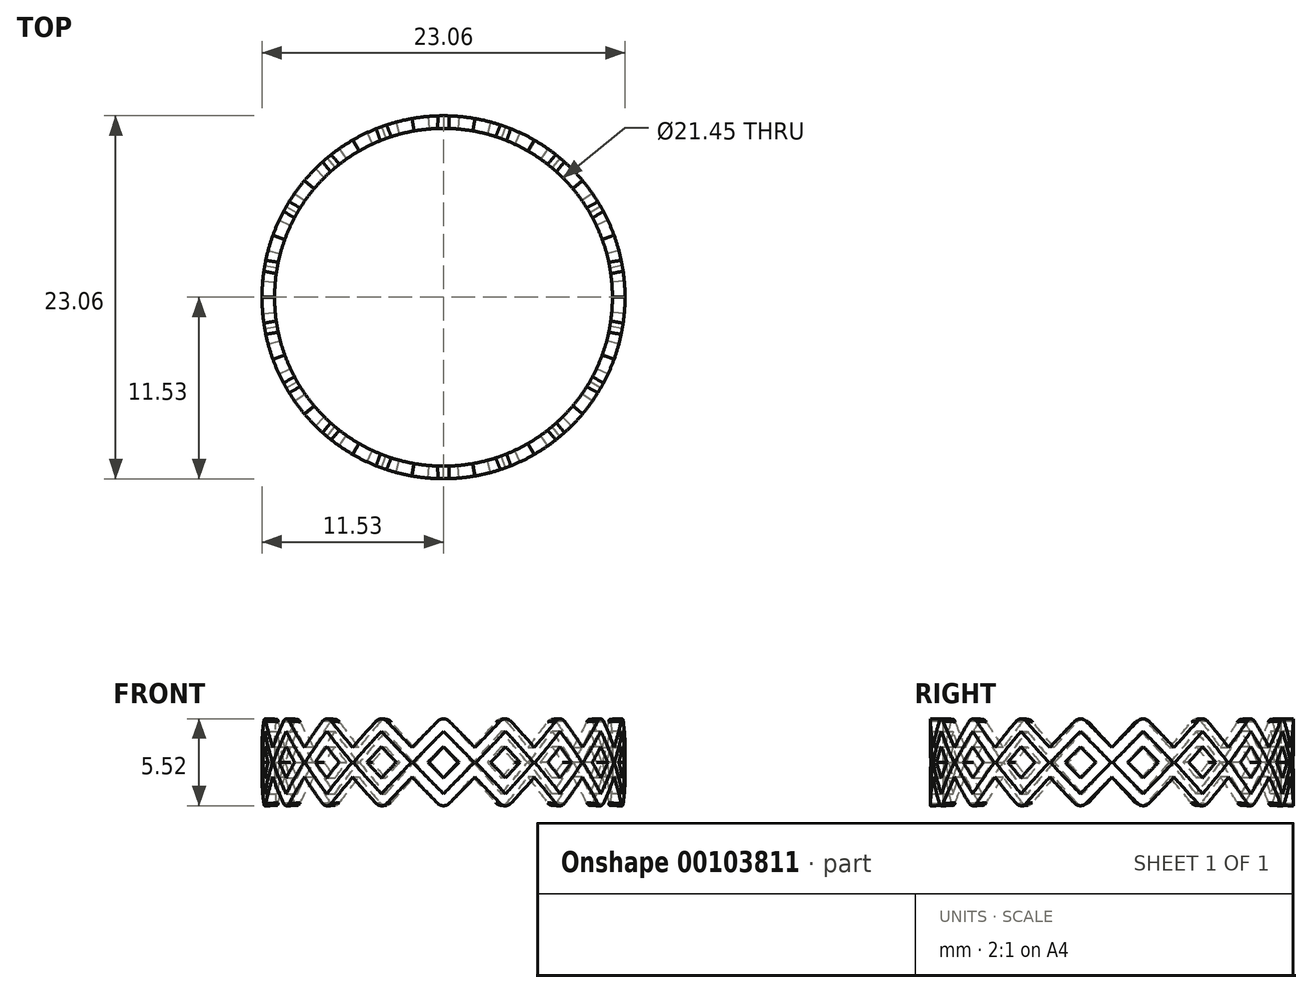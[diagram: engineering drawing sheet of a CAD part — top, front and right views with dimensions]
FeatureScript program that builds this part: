
annotation { "Feature Type Name" : "Feature", "Feature Type Description" : "" }
export const myFeature = defineFeature(function(context is Context, id is Id, definition is map)
    precondition{}
    {
        {
            var Q0;
            Q0=qCreatedBy(makeId("Front.planeOp"),FACE);
            var sketch = newSketch(context, id + "F0", { "sketchPlane" : qUnion([Q0])});
            skLineSegment(sketch, "E0", {"start": v(0, 0) * mm, "end": v(0, 10) * mm, "construction": true});
            skSolve(sketch);
        }
        {
            var Q0;
            Q0=qCreatedBy(makeId("Front.planeOp"),FACE);
            cPlane(context, id + "F1", {"entities" : qUnion([Q0]), "cplaneType" : CPlaneType.OFFSET, "offset" : 11.53 * mm, "width" : 150 * mm, "height" : 150 * mm});
        }
        {
            var Q0;
            Q0=qCreatedBy(makeId("Front.planeOp"),FACE);
            cPlane(context, id + "F2", {"entities" : qUnion([Q0]), "cplaneType" : CPlaneType.OFFSET, "offset" : 9 * mm, "width" : 150 * mm, "height" : 150 * mm});
        }
        {
            var Q0;
            Q0=qCreatedBy(makeId("Top.planeOp"),FACE);
            var sketch = newSketch(context, id + "F3", { "sketchPlane" : qUnion([Q0])});
            skLineSegment(sketch, "E1", {"start": v(0, 0) * mm, "end": v(10.03, 0) * mm, "construction": true});
            skLineSegment(sketch, "E2", {"start": v(10.03, 0) * mm, "end": v(11.53, 0) * mm, "construction": true});
            skCircle(sketch, "E3", {"center": v(0, 0) * mm, "radius": 10.03 * mm});
            skCircle(sketch, "E4", {"center": v(0, 0) * mm, "radius": 11.53 * mm});
            skSolve(sketch);
        }
        {
            var Q0;
            Q0=qCreatedBy(makeId("Top.planeOp"),FACE);
            var sketch = newSketch(context, id + "F4", { "sketchPlane" : qUnion([Q0])});
            skLineSegment(sketch, "E5", {"start": v(0, 0) * mm, "end": v(10.73, 0) * mm});
            skLineSegment(sketch, "E6", {"start": v(10.73, 0) * mm, "end": v(11.53, 0) * mm});
            skCircle(sketch, "E7", {"center": v(0, 0) * mm, "radius": 11.53 * mm});
            skCircle(sketch, "E8", {"center": v(0, 0) * mm, "radius": 10.73 * mm});
            skSolve(sketch);
        }
        {
            var Q0;
            Q0=qCreatedBy(id+"F1.planeOp",FACE);
            var sketch = newSketch(context, id + "F5", { "sketchPlane" : qUnion([Q0])});
            skLineSegment(sketch, "E9", {"start": v(-2.97, 0) * mm, "end": v(0, 2.97) * mm});
            skLineSegment(sketch, "E10", {"start": v(0, 2.97) * mm, "end": v(2.97, 0) * mm});
            skLineSegment(sketch, "E11", {"start": v(2.97, 0) * mm, "end": v(0, -2.97) * mm});
            skLineSegment(sketch, "E12", {"start": v(0, -2.97) * mm, "end": v(-2.97, 0) * mm});
            skSolve(sketch);
        }
        {
            var Q0;
            Q0=qCreatedBy(id+"F1.planeOp",FACE);
            var sketch = newSketch(context, id + "F6", { "sketchPlane" : qUnion([Q0])});
            skLineSegment(sketch, "E13", {"start": v(0, 1.96) * mm, "end": v(-1.98, -0.02) * mm});
            skLineSegment(sketch, "E14", {"start": v(-1.98, -0.02) * mm, "end": v(0, -2) * mm});
            skLineSegment(sketch, "E15", {"start": v(0, -2) * mm, "end": v(1.98, -0.02) * mm});
            skLineSegment(sketch, "E16", {"start": v(0, 1.96) * mm, "end": v(1.98, -0.02) * mm});
            skSolve(sketch);
        }
        {
            var Q0;
            Q0=qCreatedBy(id+"F1.planeOp",FACE);
            var sketch = newSketch(context, id + "F7", { "sketchPlane" : qUnion([Q0])});
            skLineSegment(sketch, "E17", {"start": v(-0.99, 0) * mm, "end": v(0, 0.99) * mm});
            skLineSegment(sketch, "E18", {"start": v(0, 0.99) * mm, "end": v(0.99, 0) * mm});
            skLineSegment(sketch, "E19", {"start": v(0.99, 0) * mm, "end": v(0, -0.99) * mm});
            skLineSegment(sketch, "E20", {"start": v(0, -0.99) * mm, "end": v(-0.99, 0) * mm});
            skSolve(sketch);
        }
        {
            var Q0;
            Q0=qCreatedBy(makeId("Top.planeOp"),FACE);
            var sketch = newSketch(context, id + "F8", { "sketchPlane" : qUnion([Q0])});
            skLineSegment(sketch, "E21", {"start": v(0, 0) * mm, "end": v(0, 0) * mm});
            skLineSegment(sketch, "E22", {"start": v(0, 0) * mm, "end": v(-0.77, -9) * mm, "construction": true});
            skLineSegment(sketch, "E23", {"start": v(0, 0) * mm, "end": v(0.77, -9) * mm, "construction": true});
            skLineSegment(sketch, "E24", {"start": v(-0.77, -9) * mm, "end": v(-0.99, -11.53) * mm, "construction": true});
            skLineSegment(sketch, "E25", {"start": v(0.77, -9) * mm, "end": v(0.99, -11.53) * mm, "construction": true});
            skSolve(sketch);
        }
        {
            var Q0;
            Q0=qCreatedBy(makeId("Top.planeOp"),FACE);
            var sketch = newSketch(context, id + "F9", { "sketchPlane" : qUnion([Q0])});
            skLineSegment(sketch, "E26", {"start": v(0, 0) * mm, "end": v(2.32, -9) * mm, "construction": true});
            skLineSegment(sketch, "E27", {"start": v(0, 0) * mm, "end": v(-2.32, -9) * mm, "construction": true});
            skLineSegment(sketch, "E28", {"start": v(2.32, -9) * mm, "end": v(2.97, -11.53) * mm, "construction": true});
            skLineSegment(sketch, "E29", {"start": v(-2.32, -9) * mm, "end": v(-2.97, -11.53) * mm, "construction": true});
            skSolve(sketch);
        }
        {
            var Q0;
            Q0=qCreatedBy(id+"F2.planeOp",FACE);
            var sketch = newSketch(context, id + "F10", { "sketchPlane" : qUnion([Q0])});
            skLineSegment(sketch, "E30", {"start": v(0, 2.97) * mm, "end": v(-2.32, 0) * mm});
            skLineSegment(sketch, "E31", {"start": v(-2.32, 0) * mm, "end": v(0, -2.97) * mm});
            skLineSegment(sketch, "E32", {"start": v(0, -2.97) * mm, "end": v(2.32, 0) * mm});
            skLineSegment(sketch, "E33", {"start": v(2.32, 0) * mm, "end": v(0, 2.97) * mm});
            skSolve(sketch);
        }
        {
            var Q0;
            Q0=qCreatedBy(id+"F2.planeOp",FACE);
            var sketch = newSketch(context, id + "F11", { "sketchPlane" : qUnion([Q0])});
            skLineSegment(sketch, "E34", {"start": v(0, 1.96) * mm, "end": v(-1.55, 0) * mm});
            skLineSegment(sketch, "E35", {"start": v(-1.55, 0) * mm, "end": v(0, -2) * mm});
            skLineSegment(sketch, "E36", {"start": v(0, -2) * mm, "end": v(1.55, 0) * mm});
            skLineSegment(sketch, "E37", {"start": v(1.55, 0) * mm, "end": v(0, 1.96) * mm});
            skSolve(sketch);
        }
        {
            var Q0;
            Q0=qCreatedBy(id+"F2.planeOp",FACE);
            var sketch = newSketch(context, id + "F12", { "sketchPlane" : qUnion([Q0])});
            skLineSegment(sketch, "E38", {"start": v(0, 0.99) * mm, "end": v(-0.77, 0) * mm});
            skLineSegment(sketch, "E39", {"start": v(-0.77, 0) * mm, "end": v(0, -0.99) * mm});
            skLineSegment(sketch, "E40", {"start": v(0, -0.99) * mm, "end": v(0.77, 0) * mm});
            skLineSegment(sketch, "E41", {"start": v(0.77, 0) * mm, "end": v(0, 0.99) * mm});
            skSolve(sketch);
        }
        {
            var Q0;
            Q0=makeQuery(id+"F5.imprint","IMPRINT",FACE,{"disambiguationData":[TD([[makeQuery(id+"F5.imprint","IMPRINT",EDGE,{"derivedFrom":sQuery(id+"F5.wireOp",EDGE,"E9")}),-1.0]])]});
            var Q1;
            Q1=makeQuery(id+"F10.imprint","IMPRINT",FACE,{"disambiguationData":[TD([[makeQuery(id+"F10.imprint","IMPRINT",EDGE,{"derivedFrom":sQuery(id+"F10.wireOp",EDGE,"E30")}),1.0]])]});
            loft(context, id + "F13", {"sheetProfilesArray" : [{ "sheetProfileEntities" : qUnion([Q0]) }, { "sheetProfileEntities" : qUnion([Q1]) }]});
        }
        {
            var Q0;
            Q0=makeQuery(id+"F6.imprint","IMPRINT",FACE,{"disambiguationData":[TD([[makeQuery(id+"F6.imprint","IMPRINT",EDGE,{"derivedFrom":sQuery(id+"F6.wireOp",EDGE,"E13")}),1.0]])]});
            var Q1;
            Q1=makeQuery(id+"F11.imprint","IMPRINT",FACE,{"disambiguationData":[TD([[makeQuery(id+"F11.imprint","IMPRINT",EDGE,{"derivedFrom":sQuery(id+"F11.wireOp",EDGE,"E34")}),1.0]])]});
            loft(context, id + "F14", {"sheetProfilesArray" : [{ "sheetProfileEntities" : qUnion([Q0]) }, { "sheetProfileEntities" : qUnion([Q1]) }]});
        }
        {
            var Q0;
            Q0 = qSketchRegion(id + "F7", true);
            var Q1;
            Q1 = qSketchRegion(id + "F12", true);
            loft(context, id + "F15", {"sheetProfilesArray" : [{ "sheetProfileEntities" : qUnion([Q0]) }, { "sheetProfileEntities" : qUnion([Q1]) }]});
        }
        {
            var Q0;
            Q0=makeQuery(id+"F13.opLoft","SWEPT_BODY",BODY,{"disambiguationData":[OSD([makeQuery(id+"F5.imprint","IMPRINT",FACE,{"disambiguationData":[TD([[makeQuery(id+"F5.imprint","IMPRINT",EDGE,{"derivedFrom":sQuery(id+"F5.wireOp",EDGE,"E9")}),-1.0]])]}),makeQuery(id+"F10.imprint","IMPRINT",FACE,{"disambiguationData":[TD([[makeQuery(id+"F10.imprint","IMPRINT",EDGE,{"derivedFrom":sQuery(id+"F10.wireOp",EDGE,"E30")}),1.0]])]})])]});
            var Q1;
            Q1=sQuery(id+"F0.wireOp",EDGE,"E0");
            circularPattern(context, id + "F16", {"entities" : qUnion([Q0]), "axis" : qUnion([Q1]), "angle" : 360 * degree, "instanceCount" : 18, "equalSpace" : true});
        }
        {
            var Q0;
            Q0=makeQuery(id+"F16.opPattern","COPY",BODY,{"derivedFrom":makeQuery(id+"F13.opLoft","SWEPT_BODY",BODY,{"disambiguationData":[OSD([makeQuery(id+"F5.imprint","IMPRINT",FACE,{"disambiguationData":[TD([[makeQuery(id+"F5.imprint","IMPRINT",EDGE,{"derivedFrom":sQuery(id+"F5.wireOp",EDGE,"E9")}),-1.0]])]}),makeQuery(id+"F10.imprint","IMPRINT",FACE,{"disambiguationData":[TD([[makeQuery(id+"F10.imprint","IMPRINT",EDGE,{"derivedFrom":sQuery(id+"F10.wireOp",EDGE,"E30")}),1.0]])]})])]}),"instanceName":"1"});
            var Q1;
            Q1=makeQuery(id+"F16.opPattern","COPY",BODY,{"derivedFrom":makeQuery(id+"F13.opLoft","SWEPT_BODY",BODY,{"disambiguationData":[OSD([makeQuery(id+"F5.imprint","IMPRINT",FACE,{"disambiguationData":[TD([[makeQuery(id+"F5.imprint","IMPRINT",EDGE,{"derivedFrom":sQuery(id+"F5.wireOp",EDGE,"E9")}),-1.0]])]}),makeQuery(id+"F10.imprint","IMPRINT",FACE,{"disambiguationData":[TD([[makeQuery(id+"F10.imprint","IMPRINT",EDGE,{"derivedFrom":sQuery(id+"F10.wireOp",EDGE,"E30")}),1.0]])]})])]}),"instanceName":"2"});
            var Q2;
            Q2=makeQuery(id+"F16.opPattern","COPY",BODY,{"derivedFrom":makeQuery(id+"F13.opLoft","SWEPT_BODY",BODY,{"disambiguationData":[OSD([makeQuery(id+"F5.imprint","IMPRINT",FACE,{"disambiguationData":[TD([[makeQuery(id+"F5.imprint","IMPRINT",EDGE,{"derivedFrom":sQuery(id+"F5.wireOp",EDGE,"E9")}),-1.0]])]}),makeQuery(id+"F10.imprint","IMPRINT",FACE,{"disambiguationData":[TD([[makeQuery(id+"F10.imprint","IMPRINT",EDGE,{"derivedFrom":sQuery(id+"F10.wireOp",EDGE,"E30")}),1.0]])]})])]}),"instanceName":"3"});
            var Q3;
            Q3=makeQuery(id+"F16.opPattern","COPY",BODY,{"derivedFrom":makeQuery(id+"F13.opLoft","SWEPT_BODY",BODY,{"disambiguationData":[OSD([makeQuery(id+"F5.imprint","IMPRINT",FACE,{"disambiguationData":[TD([[makeQuery(id+"F5.imprint","IMPRINT",EDGE,{"derivedFrom":sQuery(id+"F5.wireOp",EDGE,"E9")}),-1.0]])]}),makeQuery(id+"F10.imprint","IMPRINT",FACE,{"disambiguationData":[TD([[makeQuery(id+"F10.imprint","IMPRINT",EDGE,{"derivedFrom":sQuery(id+"F10.wireOp",EDGE,"E30")}),1.0]])]})])]}),"instanceName":"4"});
            var Q4;
            Q4=makeQuery(id+"F16.opPattern","COPY",BODY,{"derivedFrom":makeQuery(id+"F13.opLoft","SWEPT_BODY",BODY,{"disambiguationData":[OSD([makeQuery(id+"F5.imprint","IMPRINT",FACE,{"disambiguationData":[TD([[makeQuery(id+"F5.imprint","IMPRINT",EDGE,{"derivedFrom":sQuery(id+"F5.wireOp",EDGE,"E9")}),-1.0]])]}),makeQuery(id+"F10.imprint","IMPRINT",FACE,{"disambiguationData":[TD([[makeQuery(id+"F10.imprint","IMPRINT",EDGE,{"derivedFrom":sQuery(id+"F10.wireOp",EDGE,"E30")}),1.0]])]})])]}),"instanceName":"5"});
            var Q5;
            Q5=makeQuery(id+"F16.opPattern","COPY",BODY,{"derivedFrom":makeQuery(id+"F13.opLoft","SWEPT_BODY",BODY,{"disambiguationData":[OSD([makeQuery(id+"F5.imprint","IMPRINT",FACE,{"disambiguationData":[TD([[makeQuery(id+"F5.imprint","IMPRINT",EDGE,{"derivedFrom":sQuery(id+"F5.wireOp",EDGE,"E9")}),-1.0]])]}),makeQuery(id+"F10.imprint","IMPRINT",FACE,{"disambiguationData":[TD([[makeQuery(id+"F10.imprint","IMPRINT",EDGE,{"derivedFrom":sQuery(id+"F10.wireOp",EDGE,"E30")}),1.0]])]})])]}),"instanceName":"6"});
            var Q6;
            Q6=makeQuery(id+"F16.opPattern","COPY",BODY,{"derivedFrom":makeQuery(id+"F13.opLoft","SWEPT_BODY",BODY,{"disambiguationData":[OSD([makeQuery(id+"F5.imprint","IMPRINT",FACE,{"disambiguationData":[TD([[makeQuery(id+"F5.imprint","IMPRINT",EDGE,{"derivedFrom":sQuery(id+"F5.wireOp",EDGE,"E9")}),-1.0]])]}),makeQuery(id+"F10.imprint","IMPRINT",FACE,{"disambiguationData":[TD([[makeQuery(id+"F10.imprint","IMPRINT",EDGE,{"derivedFrom":sQuery(id+"F10.wireOp",EDGE,"E30")}),1.0]])]})])]}),"instanceName":"7"});
            var Q7;
            Q7=makeQuery(id+"F16.opPattern","COPY",BODY,{"derivedFrom":makeQuery(id+"F13.opLoft","SWEPT_BODY",BODY,{"disambiguationData":[OSD([makeQuery(id+"F5.imprint","IMPRINT",FACE,{"disambiguationData":[TD([[makeQuery(id+"F5.imprint","IMPRINT",EDGE,{"derivedFrom":sQuery(id+"F5.wireOp",EDGE,"E9")}),-1.0]])]}),makeQuery(id+"F10.imprint","IMPRINT",FACE,{"disambiguationData":[TD([[makeQuery(id+"F10.imprint","IMPRINT",EDGE,{"derivedFrom":sQuery(id+"F10.wireOp",EDGE,"E30")}),1.0]])]})])]}),"instanceName":"8"});
            var Q8;
            Q8=makeQuery(id+"F16.opPattern","COPY",BODY,{"derivedFrom":makeQuery(id+"F13.opLoft","SWEPT_BODY",BODY,{"disambiguationData":[OSD([makeQuery(id+"F5.imprint","IMPRINT",FACE,{"disambiguationData":[TD([[makeQuery(id+"F5.imprint","IMPRINT",EDGE,{"derivedFrom":sQuery(id+"F5.wireOp",EDGE,"E9")}),-1.0]])]}),makeQuery(id+"F10.imprint","IMPRINT",FACE,{"disambiguationData":[TD([[makeQuery(id+"F10.imprint","IMPRINT",EDGE,{"derivedFrom":sQuery(id+"F10.wireOp",EDGE,"E30")}),1.0]])]})])]}),"instanceName":"9"});
            var Q9;
            Q9=makeQuery(id+"F16.opPattern","COPY",BODY,{"derivedFrom":makeQuery(id+"F13.opLoft","SWEPT_BODY",BODY,{"disambiguationData":[OSD([makeQuery(id+"F5.imprint","IMPRINT",FACE,{"disambiguationData":[TD([[makeQuery(id+"F5.imprint","IMPRINT",EDGE,{"derivedFrom":sQuery(id+"F5.wireOp",EDGE,"E9")}),-1.0]])]}),makeQuery(id+"F10.imprint","IMPRINT",FACE,{"disambiguationData":[TD([[makeQuery(id+"F10.imprint","IMPRINT",EDGE,{"derivedFrom":sQuery(id+"F10.wireOp",EDGE,"E30")}),1.0]])]})])]}),"instanceName":"10"});
            var Q10;
            Q10=makeQuery(id+"F16.opPattern","COPY",BODY,{"derivedFrom":makeQuery(id+"F13.opLoft","SWEPT_BODY",BODY,{"disambiguationData":[OSD([makeQuery(id+"F5.imprint","IMPRINT",FACE,{"disambiguationData":[TD([[makeQuery(id+"F5.imprint","IMPRINT",EDGE,{"derivedFrom":sQuery(id+"F5.wireOp",EDGE,"E9")}),-1.0]])]}),makeQuery(id+"F10.imprint","IMPRINT",FACE,{"disambiguationData":[TD([[makeQuery(id+"F10.imprint","IMPRINT",EDGE,{"derivedFrom":sQuery(id+"F10.wireOp",EDGE,"E30")}),1.0]])]})])]}),"instanceName":"11"});
            var Q11;
            Q11=makeQuery(id+"F16.opPattern","COPY",BODY,{"derivedFrom":makeQuery(id+"F13.opLoft","SWEPT_BODY",BODY,{"disambiguationData":[OSD([makeQuery(id+"F5.imprint","IMPRINT",FACE,{"disambiguationData":[TD([[makeQuery(id+"F5.imprint","IMPRINT",EDGE,{"derivedFrom":sQuery(id+"F5.wireOp",EDGE,"E9")}),-1.0]])]}),makeQuery(id+"F10.imprint","IMPRINT",FACE,{"disambiguationData":[TD([[makeQuery(id+"F10.imprint","IMPRINT",EDGE,{"derivedFrom":sQuery(id+"F10.wireOp",EDGE,"E30")}),1.0]])]})])]}),"instanceName":"12"});
            var Q12;
            Q12=makeQuery(id+"F16.opPattern","COPY",BODY,{"derivedFrom":makeQuery(id+"F13.opLoft","SWEPT_BODY",BODY,{"disambiguationData":[OSD([makeQuery(id+"F5.imprint","IMPRINT",FACE,{"disambiguationData":[TD([[makeQuery(id+"F5.imprint","IMPRINT",EDGE,{"derivedFrom":sQuery(id+"F5.wireOp",EDGE,"E9")}),-1.0]])]}),makeQuery(id+"F10.imprint","IMPRINT",FACE,{"disambiguationData":[TD([[makeQuery(id+"F10.imprint","IMPRINT",EDGE,{"derivedFrom":sQuery(id+"F10.wireOp",EDGE,"E30")}),1.0]])]})])]}),"instanceName":"13"});
            var Q13;
            Q13=makeQuery(id+"F16.opPattern","COPY",BODY,{"derivedFrom":makeQuery(id+"F13.opLoft","SWEPT_BODY",BODY,{"disambiguationData":[OSD([makeQuery(id+"F5.imprint","IMPRINT",FACE,{"disambiguationData":[TD([[makeQuery(id+"F5.imprint","IMPRINT",EDGE,{"derivedFrom":sQuery(id+"F5.wireOp",EDGE,"E9")}),-1.0]])]}),makeQuery(id+"F10.imprint","IMPRINT",FACE,{"disambiguationData":[TD([[makeQuery(id+"F10.imprint","IMPRINT",EDGE,{"derivedFrom":sQuery(id+"F10.wireOp",EDGE,"E30")}),1.0]])]})])]}),"instanceName":"14"});
            var Q14;
            Q14=makeQuery(id+"F16.opPattern","COPY",BODY,{"derivedFrom":makeQuery(id+"F13.opLoft","SWEPT_BODY",BODY,{"disambiguationData":[OSD([makeQuery(id+"F5.imprint","IMPRINT",FACE,{"disambiguationData":[TD([[makeQuery(id+"F5.imprint","IMPRINT",EDGE,{"derivedFrom":sQuery(id+"F5.wireOp",EDGE,"E9")}),-1.0]])]}),makeQuery(id+"F10.imprint","IMPRINT",FACE,{"disambiguationData":[TD([[makeQuery(id+"F10.imprint","IMPRINT",EDGE,{"derivedFrom":sQuery(id+"F10.wireOp",EDGE,"E30")}),1.0]])]})])]}),"instanceName":"15"});
            var Q15;
            Q15=makeQuery(id+"F16.opPattern","COPY",BODY,{"derivedFrom":makeQuery(id+"F13.opLoft","SWEPT_BODY",BODY,{"disambiguationData":[OSD([makeQuery(id+"F5.imprint","IMPRINT",FACE,{"disambiguationData":[TD([[makeQuery(id+"F5.imprint","IMPRINT",EDGE,{"derivedFrom":sQuery(id+"F5.wireOp",EDGE,"E9")}),-1.0]])]}),makeQuery(id+"F10.imprint","IMPRINT",FACE,{"disambiguationData":[TD([[makeQuery(id+"F10.imprint","IMPRINT",EDGE,{"derivedFrom":sQuery(id+"F10.wireOp",EDGE,"E30")}),1.0]])]})])]}),"instanceName":"16"});
            var Q16;
            Q16=makeQuery(id+"F16.opPattern","COPY",BODY,{"derivedFrom":makeQuery(id+"F13.opLoft","SWEPT_BODY",BODY,{"disambiguationData":[OSD([makeQuery(id+"F5.imprint","IMPRINT",FACE,{"disambiguationData":[TD([[makeQuery(id+"F5.imprint","IMPRINT",EDGE,{"derivedFrom":sQuery(id+"F5.wireOp",EDGE,"E9")}),-1.0]])]}),makeQuery(id+"F10.imprint","IMPRINT",FACE,{"disambiguationData":[TD([[makeQuery(id+"F10.imprint","IMPRINT",EDGE,{"derivedFrom":sQuery(id+"F10.wireOp",EDGE,"E30")}),1.0]])]})])]}),"instanceName":"17"});
            var Q17;
            Q17=makeQuery(id+"F13.opLoft","SWEPT_BODY",BODY,{"disambiguationData":[OSD([makeQuery(id+"F5.imprint","IMPRINT",FACE,{"disambiguationData":[TD([[makeQuery(id+"F5.imprint","IMPRINT",EDGE,{"derivedFrom":sQuery(id+"F5.wireOp",EDGE,"E9")}),-1.0]])]}),makeQuery(id+"F10.imprint","IMPRINT",FACE,{"disambiguationData":[TD([[makeQuery(id+"F10.imprint","IMPRINT",EDGE,{"derivedFrom":sQuery(id+"F10.wireOp",EDGE,"E30")}),1.0]])]})])]});
            booleanBodies(context, id + "F17", {"operationType" : BooleanOperationType.UNION, "tools" : qUnion([Q0, Q1, Q2, Q3, Q4, Q5, Q6, Q7, Q8, Q9, Q10, Q11, Q12, Q13, Q14, Q15, Q16, Q17])});
        }
        {
            var Q0;
            Q0=makeQuery(id+"F14.opLoft","SWEPT_BODY",BODY,{"disambiguationData":[OSD([makeQuery(id+"F6.imprint","IMPRINT",FACE,{"disambiguationData":[TD([[makeQuery(id+"F6.imprint","IMPRINT",EDGE,{"derivedFrom":sQuery(id+"F6.wireOp",EDGE,"E13")}),1.0]])]}),makeQuery(id+"F11.imprint","IMPRINT",FACE,{"disambiguationData":[TD([[makeQuery(id+"F11.imprint","IMPRINT",EDGE,{"derivedFrom":sQuery(id+"F11.wireOp",EDGE,"E34")}),1.0]])]})])]});
            var Q1;
            Q1=sQuery(id+"F0.wireOp",EDGE,"E0");
            circularPattern(context, id + "F18", {"entities" : qUnion([Q0]), "axis" : qUnion([Q1]), "angle" : 360 * degree, "instanceCount" : 18, "equalSpace" : true});
        }
        {
            var Q0;
            Q0=makeQuery(id+"F15.opLoft","SWEPT_BODY",BODY,{"disambiguationData":[OSD([makeQuery(id+"F7.imprint","IMPRINT",FACE,{"disambiguationData":[TD([[makeQuery(id+"F7.imprint","IMPRINT",EDGE,{"derivedFrom":sQuery(id+"F7.wireOp",EDGE,"E17")}),-1.0]])]}),makeQuery(id+"F12.imprint","IMPRINT",FACE,{"disambiguationData":[TD([[makeQuery(id+"F12.imprint","IMPRINT",EDGE,{"derivedFrom":sQuery(id+"F12.wireOp",EDGE,"E38")}),1.0]])]})])]});
            var Q1;
            Q1=sQuery(id+"F0.wireOp",EDGE,"E0");
            circularPattern(context, id + "F19", {"operationType" : NewBodyOperationType.REMOVE, "entities" : qUnion([Q0]), "axis" : qUnion([Q1]), "angle" : 360 * degree, "instanceCount" : 18, "equalSpace" : true});
        }
        {
            var Q0;
            Q0 = qSketchRegion(id + "F3", true);
            extrude(context, id + "F20", {"entities" : qUnion([Q0]), "operationType" : NewBodyOperationType.INTERSECT, "depth" : 8 * mm, "symmetric" : true});
        }
        {
            var Q0;
            Q0 = qSketchRegion(id + "F4", true);
            extrude(context, id + "F21", {"entities" : qUnion([Q0]), "operationType" : NewBodyOperationType.INTERSECT, "depth" : 8 * mm, "symmetric" : true});
        }
        {
            var Q0;
            Q0=makeQuery(id+"F18.opPattern","COPY",BODY,{"derivedFrom":makeQuery(id+"F14.opLoft","SWEPT_BODY",BODY,{"disambiguationData":[OSD([makeQuery(id+"F6.imprint","IMPRINT",FACE,{"disambiguationData":[TD([[makeQuery(id+"F6.imprint","IMPRINT",EDGE,{"derivedFrom":sQuery(id+"F6.wireOp",EDGE,"E13")}),1.0]])]}),makeQuery(id+"F11.imprint","IMPRINT",FACE,{"disambiguationData":[TD([[makeQuery(id+"F11.imprint","IMPRINT",EDGE,{"derivedFrom":sQuery(id+"F11.wireOp",EDGE,"E34")}),1.0]])]})])]}),"instanceName":"1"});
            var Q1;
            Q1=makeQuery(id+"F18.opPattern","COPY",BODY,{"derivedFrom":makeQuery(id+"F14.opLoft","SWEPT_BODY",BODY,{"disambiguationData":[OSD([makeQuery(id+"F6.imprint","IMPRINT",FACE,{"disambiguationData":[TD([[makeQuery(id+"F6.imprint","IMPRINT",EDGE,{"derivedFrom":sQuery(id+"F6.wireOp",EDGE,"E13")}),1.0]])]}),makeQuery(id+"F11.imprint","IMPRINT",FACE,{"disambiguationData":[TD([[makeQuery(id+"F11.imprint","IMPRINT",EDGE,{"derivedFrom":sQuery(id+"F11.wireOp",EDGE,"E34")}),1.0]])]})])]}),"instanceName":"2"});
            var Q2;
            Q2=makeQuery(id+"F18.opPattern","COPY",BODY,{"derivedFrom":makeQuery(id+"F14.opLoft","SWEPT_BODY",BODY,{"disambiguationData":[OSD([makeQuery(id+"F6.imprint","IMPRINT",FACE,{"disambiguationData":[TD([[makeQuery(id+"F6.imprint","IMPRINT",EDGE,{"derivedFrom":sQuery(id+"F6.wireOp",EDGE,"E13")}),1.0]])]}),makeQuery(id+"F11.imprint","IMPRINT",FACE,{"disambiguationData":[TD([[makeQuery(id+"F11.imprint","IMPRINT",EDGE,{"derivedFrom":sQuery(id+"F11.wireOp",EDGE,"E34")}),1.0]])]})])]}),"instanceName":"3"});
            var Q3;
            Q3=makeQuery(id+"F18.opPattern","COPY",BODY,{"derivedFrom":makeQuery(id+"F14.opLoft","SWEPT_BODY",BODY,{"disambiguationData":[OSD([makeQuery(id+"F6.imprint","IMPRINT",FACE,{"disambiguationData":[TD([[makeQuery(id+"F6.imprint","IMPRINT",EDGE,{"derivedFrom":sQuery(id+"F6.wireOp",EDGE,"E13")}),1.0]])]}),makeQuery(id+"F11.imprint","IMPRINT",FACE,{"disambiguationData":[TD([[makeQuery(id+"F11.imprint","IMPRINT",EDGE,{"derivedFrom":sQuery(id+"F11.wireOp",EDGE,"E34")}),1.0]])]})])]}),"instanceName":"4"});
            var Q4;
            Q4=makeQuery(id+"F18.opPattern","COPY",BODY,{"derivedFrom":makeQuery(id+"F14.opLoft","SWEPT_BODY",BODY,{"disambiguationData":[OSD([makeQuery(id+"F6.imprint","IMPRINT",FACE,{"disambiguationData":[TD([[makeQuery(id+"F6.imprint","IMPRINT",EDGE,{"derivedFrom":sQuery(id+"F6.wireOp",EDGE,"E13")}),1.0]])]}),makeQuery(id+"F11.imprint","IMPRINT",FACE,{"disambiguationData":[TD([[makeQuery(id+"F11.imprint","IMPRINT",EDGE,{"derivedFrom":sQuery(id+"F11.wireOp",EDGE,"E34")}),1.0]])]})])]}),"instanceName":"5"});
            var Q5;
            Q5=makeQuery(id+"F18.opPattern","COPY",BODY,{"derivedFrom":makeQuery(id+"F14.opLoft","SWEPT_BODY",BODY,{"disambiguationData":[OSD([makeQuery(id+"F6.imprint","IMPRINT",FACE,{"disambiguationData":[TD([[makeQuery(id+"F6.imprint","IMPRINT",EDGE,{"derivedFrom":sQuery(id+"F6.wireOp",EDGE,"E13")}),1.0]])]}),makeQuery(id+"F11.imprint","IMPRINT",FACE,{"disambiguationData":[TD([[makeQuery(id+"F11.imprint","IMPRINT",EDGE,{"derivedFrom":sQuery(id+"F11.wireOp",EDGE,"E34")}),1.0]])]})])]}),"instanceName":"6"});
            var Q6;
            Q6=makeQuery(id+"F18.opPattern","COPY",BODY,{"derivedFrom":makeQuery(id+"F14.opLoft","SWEPT_BODY",BODY,{"disambiguationData":[OSD([makeQuery(id+"F6.imprint","IMPRINT",FACE,{"disambiguationData":[TD([[makeQuery(id+"F6.imprint","IMPRINT",EDGE,{"derivedFrom":sQuery(id+"F6.wireOp",EDGE,"E13")}),1.0]])]}),makeQuery(id+"F11.imprint","IMPRINT",FACE,{"disambiguationData":[TD([[makeQuery(id+"F11.imprint","IMPRINT",EDGE,{"derivedFrom":sQuery(id+"F11.wireOp",EDGE,"E34")}),1.0]])]})])]}),"instanceName":"7"});
            var Q7;
            Q7=makeQuery(id+"F18.opPattern","COPY",BODY,{"derivedFrom":makeQuery(id+"F14.opLoft","SWEPT_BODY",BODY,{"disambiguationData":[OSD([makeQuery(id+"F6.imprint","IMPRINT",FACE,{"disambiguationData":[TD([[makeQuery(id+"F6.imprint","IMPRINT",EDGE,{"derivedFrom":sQuery(id+"F6.wireOp",EDGE,"E13")}),1.0]])]}),makeQuery(id+"F11.imprint","IMPRINT",FACE,{"disambiguationData":[TD([[makeQuery(id+"F11.imprint","IMPRINT",EDGE,{"derivedFrom":sQuery(id+"F11.wireOp",EDGE,"E34")}),1.0]])]})])]}),"instanceName":"8"});
            var Q8;
            Q8=makeQuery(id+"F18.opPattern","COPY",BODY,{"derivedFrom":makeQuery(id+"F14.opLoft","SWEPT_BODY",BODY,{"disambiguationData":[OSD([makeQuery(id+"F6.imprint","IMPRINT",FACE,{"disambiguationData":[TD([[makeQuery(id+"F6.imprint","IMPRINT",EDGE,{"derivedFrom":sQuery(id+"F6.wireOp",EDGE,"E13")}),1.0]])]}),makeQuery(id+"F11.imprint","IMPRINT",FACE,{"disambiguationData":[TD([[makeQuery(id+"F11.imprint","IMPRINT",EDGE,{"derivedFrom":sQuery(id+"F11.wireOp",EDGE,"E34")}),1.0]])]})])]}),"instanceName":"9"});
            var Q9;
            Q9=makeQuery(id+"F18.opPattern","COPY",BODY,{"derivedFrom":makeQuery(id+"F14.opLoft","SWEPT_BODY",BODY,{"disambiguationData":[OSD([makeQuery(id+"F6.imprint","IMPRINT",FACE,{"disambiguationData":[TD([[makeQuery(id+"F6.imprint","IMPRINT",EDGE,{"derivedFrom":sQuery(id+"F6.wireOp",EDGE,"E13")}),1.0]])]}),makeQuery(id+"F11.imprint","IMPRINT",FACE,{"disambiguationData":[TD([[makeQuery(id+"F11.imprint","IMPRINT",EDGE,{"derivedFrom":sQuery(id+"F11.wireOp",EDGE,"E34")}),1.0]])]})])]}),"instanceName":"10"});
            var Q10;
            Q10=makeQuery(id+"F18.opPattern","COPY",BODY,{"derivedFrom":makeQuery(id+"F14.opLoft","SWEPT_BODY",BODY,{"disambiguationData":[OSD([makeQuery(id+"F6.imprint","IMPRINT",FACE,{"disambiguationData":[TD([[makeQuery(id+"F6.imprint","IMPRINT",EDGE,{"derivedFrom":sQuery(id+"F6.wireOp",EDGE,"E13")}),1.0]])]}),makeQuery(id+"F11.imprint","IMPRINT",FACE,{"disambiguationData":[TD([[makeQuery(id+"F11.imprint","IMPRINT",EDGE,{"derivedFrom":sQuery(id+"F11.wireOp",EDGE,"E34")}),1.0]])]})])]}),"instanceName":"11"});
            var Q11;
            Q11=makeQuery(id+"F18.opPattern","COPY",BODY,{"derivedFrom":makeQuery(id+"F14.opLoft","SWEPT_BODY",BODY,{"disambiguationData":[OSD([makeQuery(id+"F6.imprint","IMPRINT",FACE,{"disambiguationData":[TD([[makeQuery(id+"F6.imprint","IMPRINT",EDGE,{"derivedFrom":sQuery(id+"F6.wireOp",EDGE,"E13")}),1.0]])]}),makeQuery(id+"F11.imprint","IMPRINT",FACE,{"disambiguationData":[TD([[makeQuery(id+"F11.imprint","IMPRINT",EDGE,{"derivedFrom":sQuery(id+"F11.wireOp",EDGE,"E34")}),1.0]])]})])]}),"instanceName":"12"});
            var Q12;
            Q12=makeQuery(id+"F18.opPattern","COPY",BODY,{"derivedFrom":makeQuery(id+"F14.opLoft","SWEPT_BODY",BODY,{"disambiguationData":[OSD([makeQuery(id+"F6.imprint","IMPRINT",FACE,{"disambiguationData":[TD([[makeQuery(id+"F6.imprint","IMPRINT",EDGE,{"derivedFrom":sQuery(id+"F6.wireOp",EDGE,"E13")}),1.0]])]}),makeQuery(id+"F11.imprint","IMPRINT",FACE,{"disambiguationData":[TD([[makeQuery(id+"F11.imprint","IMPRINT",EDGE,{"derivedFrom":sQuery(id+"F11.wireOp",EDGE,"E34")}),1.0]])]})])]}),"instanceName":"13"});
            var Q13;
            Q13=makeQuery(id+"F18.opPattern","COPY",BODY,{"derivedFrom":makeQuery(id+"F14.opLoft","SWEPT_BODY",BODY,{"disambiguationData":[OSD([makeQuery(id+"F6.imprint","IMPRINT",FACE,{"disambiguationData":[TD([[makeQuery(id+"F6.imprint","IMPRINT",EDGE,{"derivedFrom":sQuery(id+"F6.wireOp",EDGE,"E13")}),1.0]])]}),makeQuery(id+"F11.imprint","IMPRINT",FACE,{"disambiguationData":[TD([[makeQuery(id+"F11.imprint","IMPRINT",EDGE,{"derivedFrom":sQuery(id+"F11.wireOp",EDGE,"E34")}),1.0]])]})])]}),"instanceName":"14"});
            var Q14;
            Q14=makeQuery(id+"F18.opPattern","COPY",BODY,{"derivedFrom":makeQuery(id+"F14.opLoft","SWEPT_BODY",BODY,{"disambiguationData":[OSD([makeQuery(id+"F6.imprint","IMPRINT",FACE,{"disambiguationData":[TD([[makeQuery(id+"F6.imprint","IMPRINT",EDGE,{"derivedFrom":sQuery(id+"F6.wireOp",EDGE,"E13")}),1.0]])]}),makeQuery(id+"F11.imprint","IMPRINT",FACE,{"disambiguationData":[TD([[makeQuery(id+"F11.imprint","IMPRINT",EDGE,{"derivedFrom":sQuery(id+"F11.wireOp",EDGE,"E34")}),1.0]])]})])]}),"instanceName":"15"});
            var Q15;
            Q15=makeQuery(id+"F18.opPattern","COPY",BODY,{"derivedFrom":makeQuery(id+"F14.opLoft","SWEPT_BODY",BODY,{"disambiguationData":[OSD([makeQuery(id+"F6.imprint","IMPRINT",FACE,{"disambiguationData":[TD([[makeQuery(id+"F6.imprint","IMPRINT",EDGE,{"derivedFrom":sQuery(id+"F6.wireOp",EDGE,"E13")}),1.0]])]}),makeQuery(id+"F11.imprint","IMPRINT",FACE,{"disambiguationData":[TD([[makeQuery(id+"F11.imprint","IMPRINT",EDGE,{"derivedFrom":sQuery(id+"F11.wireOp",EDGE,"E34")}),1.0]])]})])]}),"instanceName":"16"});
            var Q16;
            Q16=makeQuery(id+"F18.opPattern","COPY",BODY,{"derivedFrom":makeQuery(id+"F14.opLoft","SWEPT_BODY",BODY,{"disambiguationData":[OSD([makeQuery(id+"F6.imprint","IMPRINT",FACE,{"disambiguationData":[TD([[makeQuery(id+"F6.imprint","IMPRINT",EDGE,{"derivedFrom":sQuery(id+"F6.wireOp",EDGE,"E13")}),1.0]])]}),makeQuery(id+"F11.imprint","IMPRINT",FACE,{"disambiguationData":[TD([[makeQuery(id+"F11.imprint","IMPRINT",EDGE,{"derivedFrom":sQuery(id+"F11.wireOp",EDGE,"E34")}),1.0]])]})])]}),"instanceName":"17"});
            var Q17;
            Q17=makeQuery(id+"F14.opLoft","SWEPT_BODY",BODY,{"disambiguationData":[OSD([makeQuery(id+"F6.imprint","IMPRINT",FACE,{"disambiguationData":[TD([[makeQuery(id+"F6.imprint","IMPRINT",EDGE,{"derivedFrom":sQuery(id+"F6.wireOp",EDGE,"E13")}),1.0]])]}),makeQuery(id+"F11.imprint","IMPRINT",FACE,{"disambiguationData":[TD([[makeQuery(id+"F11.imprint","IMPRINT",EDGE,{"derivedFrom":sQuery(id+"F11.wireOp",EDGE,"E34")}),1.0]])]})])]});
            var Q18;
            Q18=makeQuery(id+"F16.opPattern","COPY",BODY,{"derivedFrom":makeQuery(id+"F13.opLoft","SWEPT_BODY",BODY,{"disambiguationData":[OSD([makeQuery(id+"F5.imprint","IMPRINT",FACE,{"disambiguationData":[TD([[makeQuery(id+"F5.imprint","IMPRINT",EDGE,{"derivedFrom":sQuery(id+"F5.wireOp",EDGE,"E9")}),-1.0]])]}),makeQuery(id+"F10.imprint","IMPRINT",FACE,{"disambiguationData":[TD([[makeQuery(id+"F10.imprint","IMPRINT",EDGE,{"derivedFrom":sQuery(id+"F10.wireOp",EDGE,"E30")}),1.0]])]})])]}),"instanceName":"1"});
            booleanBodies(context, id + "F22", {"operationType" : BooleanOperationType.SUBTRACTION, "tools" : qUnion([Q0, Q1, Q2, Q3, Q4, Q5, Q6, Q7, Q8, Q9, Q10, Q11, Q12, Q13, Q14, Q15, Q16, Q17]), "targets" : qUnion([Q18]), "keepTools" : true});
        }
        {
            var Q0;
            {var subQ0=sQuery(id+"F10.wireOp",EDGE,"E30");var subQ2=sQuery(id+"F10.wireOp",EDGE,"E32");var subQ3=sQuery(id+"F10.wireOp",EDGE,"E33");var subQ4=makeQuery(id+"F13.opLoft","CAP_FACE",FACE,{"disambiguationData":[OSD([makeQuery(id+"F10.imprint","IMPRINT",FACE,{"disambiguationData":[TD([[makeQuery(id+"F10.imprint","IMPRINT",EDGE,{"derivedFrom":subQ0}),1.0]])]})])],"isStart":true});var subQ5=sQuery(id+"F5.wireOp",EDGE,"E9");var subQ6=sQuery(id+"F5.wireOp",EDGE,"E10");var subQ7=sQuery(id+"F5.wireOp",EDGE,"E11");var subQ10=makeQuery(id+"F16.opPattern","COPY",FACE,{"derivedFrom":makeQuery(id+"F13.opLoft","SWEPT_FACE",FACE,{"disambiguationData":[OSD([subQ5,subQ6,subQ7,subQ0,subQ2,subQ3])]}),"instanceName":"3"});Q0=makeQuery(id+"F20.boolean.opBoolean","INTERSECT",EDGE,{"derivedFrom":[makeQuery(id+"F17.opBoolean","SPLIT",FACE,{"disambiguationData":[TD([makeQuery(id+"F16.opPattern","COPY",FACE,{"derivedFrom":subQ4,"instanceName":"3"})])],"derivedFrom":subQ10}),makeQuery(id+"F20.boolean.toolComplement.opBoolean","COPY",FACE,{"derivedFrom":makeQuery(id+"F20.opExtrude","SWEPT_FACE",FACE,{"disambiguationData":[OSD([sQuery(id+"F3.wireOp",EDGE,"E4")])]})})]});}
            var Q1;
            {var subQ0=sQuery(id+"F10.wireOp",EDGE,"E30");var subQ1=sQuery(id+"F10.wireOp",EDGE,"E31");var subQ3=sQuery(id+"F10.wireOp",EDGE,"E33");var subQ4=makeQuery(id+"F13.opLoft","CAP_FACE",FACE,{"disambiguationData":[OSD([makeQuery(id+"F10.imprint","IMPRINT",FACE,{"disambiguationData":[TD([[makeQuery(id+"F10.imprint","IMPRINT",EDGE,{"derivedFrom":subQ0}),1.0]])]})])],"isStart":true});var subQ5=sQuery(id+"F5.wireOp",EDGE,"E12");var subQ6=sQuery(id+"F5.wireOp",EDGE,"E10");var subQ7=sQuery(id+"F5.wireOp",EDGE,"E9");var subQ8=makeQuery(id+"F16.opPattern","COPY",FACE,{"derivedFrom":makeQuery(id+"F13.opLoft","SWEPT_FACE",FACE,{"disambiguationData":[OSD([subQ7,subQ6,subQ5,subQ0,subQ1,subQ3])]}),"instanceName":"4"});Q1=makeQuery(id+"F20.boolean.opBoolean","INTERSECT",EDGE,{"derivedFrom":[makeQuery(id+"F17.opBoolean","SPLIT",FACE,{"disambiguationData":[TD([makeQuery(id+"F16.opPattern","COPY",FACE,{"derivedFrom":subQ4,"instanceName":"3"})])],"derivedFrom":subQ8}),makeQuery(id+"F20.boolean.toolComplement.opBoolean","COPY",FACE,{"derivedFrom":makeQuery(id+"F20.opExtrude","SWEPT_FACE",FACE,{"disambiguationData":[OSD([sQuery(id+"F3.wireOp",EDGE,"E4")])]})})]});}
            var Q2;
            Q2=makeQuery(id+"F16.opPattern","COPY",EDGE,{"derivedFrom":makeQuery(id+"F13.opLoft","SWEPT_EDGE",EDGE,{"disambiguationData":[OSD([sQuery(id+"F5.wireOp",EDGE,"E9"),sQuery(id+"F5.wireOp",EDGE,"E10"),sQuery(id+"F10.wireOp",EDGE,"E30"),sQuery(id+"F10.wireOp",EDGE,"E33")])]}),"instanceName":"4"});
            var Q3;
            Q3=makeQuery(id+"F16.opPattern","COPY",EDGE,{"derivedFrom":makeQuery(id+"F13.opLoft","SWEPT_EDGE",EDGE,{"disambiguationData":[OSD([sQuery(id+"F5.wireOp",EDGE,"E9"),sQuery(id+"F5.wireOp",EDGE,"E10"),sQuery(id+"F10.wireOp",EDGE,"E30"),sQuery(id+"F10.wireOp",EDGE,"E33")])]}),"instanceName":"3"});
            var Q4;
            {var subQ0=sQuery(id+"F10.wireOp",EDGE,"E30");var subQ1=sQuery(id+"F10.wireOp",EDGE,"E31");var subQ3=sQuery(id+"F10.wireOp",EDGE,"E33");var subQ4=makeQuery(id+"F13.opLoft","CAP_FACE",FACE,{"disambiguationData":[OSD([makeQuery(id+"F10.imprint","IMPRINT",FACE,{"disambiguationData":[TD([[makeQuery(id+"F10.imprint","IMPRINT",EDGE,{"derivedFrom":subQ0}),1.0]])]})])],"isStart":true});var subQ5=sQuery(id+"F5.wireOp",EDGE,"E12");var subQ6=sQuery(id+"F5.wireOp",EDGE,"E10");var subQ7=sQuery(id+"F5.wireOp",EDGE,"E9");var subQ8=makeQuery(id+"F16.opPattern","COPY",FACE,{"derivedFrom":makeQuery(id+"F13.opLoft","SWEPT_FACE",FACE,{"disambiguationData":[OSD([subQ7,subQ6,subQ5,subQ0,subQ1,subQ3])]}),"instanceName":"3"});Q4=makeQuery(id+"F20.boolean.opBoolean","INTERSECT",EDGE,{"derivedFrom":[makeQuery(id+"F17.opBoolean","SPLIT",FACE,{"disambiguationData":[TD([makeQuery(id+"F16.opPattern","COPY",FACE,{"derivedFrom":subQ4,"instanceName":"2"})])],"derivedFrom":subQ8}),makeQuery(id+"F20.boolean.toolComplement.opBoolean","COPY",FACE,{"derivedFrom":makeQuery(id+"F20.opExtrude","SWEPT_FACE",FACE,{"disambiguationData":[OSD([sQuery(id+"F3.wireOp",EDGE,"E4")])]})})]});}
            var Q5;
            {var subQ0=sQuery(id+"F5.wireOp",EDGE,"E9");var subQ2=sQuery(id+"F5.wireOp",EDGE,"E11");var subQ3=sQuery(id+"F5.wireOp",EDGE,"E12");var subQ6=sQuery(id+"F10.wireOp",EDGE,"E32");var subQ7=sQuery(id+"F10.wireOp",EDGE,"E31");var subQ9=sQuery(id+"F10.wireOp",EDGE,"E30");var subQ10=makeQuery(id+"F16.opPattern","COPY",FACE,{"derivedFrom":makeQuery(id+"F13.opLoft","SWEPT_FACE",FACE,{"disambiguationData":[OSD([subQ0,subQ2,subQ3,subQ9,subQ7,subQ6])]}),"instanceName":"3"});var subQ11=makeQuery(id+"F13.opLoft","CAP_FACE",FACE,{"disambiguationData":[OSD([makeQuery(id+"F10.imprint","IMPRINT",FACE,{"disambiguationData":[TD([[makeQuery(id+"F10.imprint","IMPRINT",EDGE,{"derivedFrom":subQ9}),1.0]])]})])],"isStart":true});Q5=makeQuery(id+"F20.boolean.opBoolean","INTERSECT",EDGE,{"derivedFrom":[makeQuery(id+"F17.opBoolean","SPLIT",FACE,{"disambiguationData":[TD([makeQuery(id+"F16.opPattern","COPY",FACE,{"derivedFrom":subQ11,"instanceName":"2"})])],"derivedFrom":subQ10}),makeQuery(id+"F20.boolean.toolComplement.opBoolean","COPY",FACE,{"derivedFrom":makeQuery(id+"F20.opExtrude","SWEPT_FACE",FACE,{"disambiguationData":[OSD([sQuery(id+"F3.wireOp",EDGE,"E4")])]})})]});}
            var Q6;
            {var subQ1=sQuery(id+"F5.wireOp",EDGE,"E10");var subQ2=sQuery(id+"F5.wireOp",EDGE,"E11");var subQ3=sQuery(id+"F5.wireOp",EDGE,"E12");var subQ5=sQuery(id+"F10.wireOp",EDGE,"E30");var subQ6=sQuery(id+"F10.wireOp",EDGE,"E31");var subQ7=sQuery(id+"F10.wireOp",EDGE,"E32");var subQ8=sQuery(id+"F10.wireOp",EDGE,"E33");var subQ9=makeQuery(id+"F13.opLoft","CAP_FACE",FACE,{"disambiguationData":[OSD([makeQuery(id+"F10.imprint","IMPRINT",FACE,{"disambiguationData":[TD([[makeQuery(id+"F10.imprint","IMPRINT",EDGE,{"derivedFrom":subQ5}),1.0]])]})])],"isStart":true});var subQ10=makeQuery(id+"F16.opPattern","COPY",FACE,{"derivedFrom":makeQuery(id+"F13.opLoft","SWEPT_FACE",FACE,{"disambiguationData":[OSD([subQ1,subQ2,subQ3,subQ6,subQ7,subQ8])]}),"instanceName":"3"});Q6=makeQuery(id+"F20.boolean.opBoolean","INTERSECT",EDGE,{"derivedFrom":[makeQuery(id+"F17.opBoolean","SPLIT",FACE,{"disambiguationData":[TD([makeQuery(id+"F16.opPattern","COPY",FACE,{"derivedFrom":subQ9,"instanceName":"3"})])],"derivedFrom":subQ10}),makeQuery(id+"F20.boolean.toolComplement.opBoolean","COPY",FACE,{"derivedFrom":makeQuery(id+"F20.opExtrude","SWEPT_FACE",FACE,{"disambiguationData":[OSD([sQuery(id+"F3.wireOp",EDGE,"E4")])]})})]});}
            var Q7;
            Q7=makeQuery(id+"F16.opPattern","COPY",EDGE,{"derivedFrom":makeQuery(id+"F13.opLoft","SWEPT_EDGE",EDGE,{"disambiguationData":[OSD([sQuery(id+"F5.wireOp",EDGE,"E11"),sQuery(id+"F5.wireOp",EDGE,"E12"),sQuery(id+"F10.wireOp",EDGE,"E31"),sQuery(id+"F10.wireOp",EDGE,"E32")])]}),"instanceName":"3"});
            var Q8;
            {var subQ0=sQuery(id+"F10.wireOp",EDGE,"E30");var subQ2=sQuery(id+"F10.wireOp",EDGE,"E32");var subQ3=sQuery(id+"F10.wireOp",EDGE,"E33");var subQ4=makeQuery(id+"F13.opLoft","CAP_FACE",FACE,{"disambiguationData":[OSD([makeQuery(id+"F10.imprint","IMPRINT",FACE,{"disambiguationData":[TD([[makeQuery(id+"F10.imprint","IMPRINT",EDGE,{"derivedFrom":subQ0}),1.0]])]})])],"isStart":true});var subQ5=sQuery(id+"F5.wireOp",EDGE,"E11");var subQ6=sQuery(id+"F5.wireOp",EDGE,"E10");var subQ7=sQuery(id+"F5.wireOp",EDGE,"E9");var subQ8=makeQuery(id+"F16.opPattern","COPY",FACE,{"derivedFrom":makeQuery(id+"F13.opLoft","SWEPT_FACE",FACE,{"disambiguationData":[OSD([subQ7,subQ6,subQ5,subQ0,subQ2,subQ3])]}),"instanceName":"4"});Q8=makeQuery(id+"F20.boolean.opBoolean","INTERSECT",EDGE,{"derivedFrom":[makeQuery(id+"F17.opBoolean","SPLIT",FACE,{"disambiguationData":[TD([makeQuery(id+"F16.opPattern","COPY",FACE,{"derivedFrom":subQ4,"instanceName":"4"})])],"derivedFrom":subQ8}),makeQuery(id+"F20.boolean.toolComplement.opBoolean","COPY",FACE,{"derivedFrom":makeQuery(id+"F20.opExtrude","SWEPT_FACE",FACE,{"disambiguationData":[OSD([sQuery(id+"F3.wireOp",EDGE,"E4")])]})})]});}
            var Q9;
            {var subQ0=sQuery(id+"F10.wireOp",EDGE,"E30");var subQ1=sQuery(id+"F10.wireOp",EDGE,"E31");var subQ3=sQuery(id+"F10.wireOp",EDGE,"E33");var subQ4=makeQuery(id+"F13.opLoft","CAP_FACE",FACE,{"disambiguationData":[OSD([makeQuery(id+"F10.imprint","IMPRINT",FACE,{"disambiguationData":[TD([[makeQuery(id+"F10.imprint","IMPRINT",EDGE,{"derivedFrom":subQ0}),1.0]])]})])],"isStart":true});var subQ6=sQuery(id+"F5.wireOp",EDGE,"E10");var subQ7=sQuery(id+"F5.wireOp",EDGE,"E9");var subQ9=sQuery(id+"F5.wireOp",EDGE,"E12");var subQ10=makeQuery(id+"F16.opPattern","COPY",FACE,{"derivedFrom":makeQuery(id+"F13.opLoft","SWEPT_FACE",FACE,{"disambiguationData":[OSD([subQ7,subQ6,subQ9,subQ0,subQ1,subQ3])]}),"instanceName":"5"});Q9=makeQuery(id+"F20.boolean.opBoolean","INTERSECT",EDGE,{"derivedFrom":[makeQuery(id+"F17.opBoolean","SPLIT",FACE,{"disambiguationData":[TD([makeQuery(id+"F16.opPattern","COPY",FACE,{"derivedFrom":subQ4,"instanceName":"4"})])],"derivedFrom":subQ10}),makeQuery(id+"F20.boolean.toolComplement.opBoolean","COPY",FACE,{"derivedFrom":makeQuery(id+"F20.opExtrude","SWEPT_FACE",FACE,{"disambiguationData":[OSD([sQuery(id+"F3.wireOp",EDGE,"E4")])]})})]});}
            var Q10;
            Q10=makeQuery(id+"F16.opPattern","COPY",EDGE,{"derivedFrom":makeQuery(id+"F13.opLoft","SWEPT_EDGE",EDGE,{"disambiguationData":[OSD([sQuery(id+"F5.wireOp",EDGE,"E9"),sQuery(id+"F5.wireOp",EDGE,"E10"),sQuery(id+"F10.wireOp",EDGE,"E30"),sQuery(id+"F10.wireOp",EDGE,"E33")])]}),"instanceName":"5"});
            var Q11;
            {var subQ0=sQuery(id+"F10.wireOp",EDGE,"E30");var subQ2=sQuery(id+"F10.wireOp",EDGE,"E32");var subQ3=sQuery(id+"F10.wireOp",EDGE,"E33");var subQ4=makeQuery(id+"F13.opLoft","CAP_FACE",FACE,{"disambiguationData":[OSD([makeQuery(id+"F10.imprint","IMPRINT",FACE,{"disambiguationData":[TD([[makeQuery(id+"F10.imprint","IMPRINT",EDGE,{"derivedFrom":subQ0}),1.0]])]})])],"isStart":true});var subQ6=sQuery(id+"F5.wireOp",EDGE,"E10");var subQ7=sQuery(id+"F5.wireOp",EDGE,"E9");var subQ9=sQuery(id+"F5.wireOp",EDGE,"E11");var subQ11=makeQuery(id+"F16.opPattern","COPY",FACE,{"derivedFrom":makeQuery(id+"F13.opLoft","SWEPT_FACE",FACE,{"disambiguationData":[OSD([subQ7,subQ6,subQ9,subQ0,subQ2,subQ3])]}),"instanceName":"5"});Q11=makeQuery(id+"F20.boolean.opBoolean","INTERSECT",EDGE,{"derivedFrom":[makeQuery(id+"F17.opBoolean","SPLIT",FACE,{"disambiguationData":[TD([makeQuery(id+"F16.opPattern","COPY",FACE,{"derivedFrom":subQ4,"instanceName":"5"})])],"derivedFrom":subQ11}),makeQuery(id+"F20.boolean.toolComplement.opBoolean","COPY",FACE,{"derivedFrom":makeQuery(id+"F20.opExtrude","SWEPT_FACE",FACE,{"disambiguationData":[OSD([sQuery(id+"F3.wireOp",EDGE,"E4")])]})})]});}
            var Q12;
            {var subQ0=sQuery(id+"F5.wireOp",EDGE,"E9");var subQ2=sQuery(id+"F5.wireOp",EDGE,"E11");var subQ3=sQuery(id+"F5.wireOp",EDGE,"E12");var subQ6=sQuery(id+"F10.wireOp",EDGE,"E32");var subQ7=sQuery(id+"F10.wireOp",EDGE,"E31");var subQ9=sQuery(id+"F10.wireOp",EDGE,"E30");var subQ10=makeQuery(id+"F16.opPattern","COPY",FACE,{"derivedFrom":makeQuery(id+"F13.opLoft","SWEPT_FACE",FACE,{"disambiguationData":[OSD([subQ0,subQ2,subQ3,subQ9,subQ7,subQ6])]}),"instanceName":"4"});var subQ11=makeQuery(id+"F13.opLoft","CAP_FACE",FACE,{"disambiguationData":[OSD([makeQuery(id+"F10.imprint","IMPRINT",FACE,{"disambiguationData":[TD([[makeQuery(id+"F10.imprint","IMPRINT",EDGE,{"derivedFrom":subQ9}),1.0]])]})])],"isStart":true});Q12=makeQuery(id+"F20.boolean.opBoolean","INTERSECT",EDGE,{"derivedFrom":[makeQuery(id+"F17.opBoolean","SPLIT",FACE,{"disambiguationData":[TD([makeQuery(id+"F16.opPattern","COPY",FACE,{"derivedFrom":subQ11,"instanceName":"3"})])],"derivedFrom":subQ10}),makeQuery(id+"F20.boolean.toolComplement.opBoolean","COPY",FACE,{"derivedFrom":makeQuery(id+"F20.opExtrude","SWEPT_FACE",FACE,{"disambiguationData":[OSD([sQuery(id+"F3.wireOp",EDGE,"E4")])]})})]});}
            var Q13;
            {var subQ1=sQuery(id+"F5.wireOp",EDGE,"E10");var subQ2=sQuery(id+"F5.wireOp",EDGE,"E11");var subQ3=sQuery(id+"F5.wireOp",EDGE,"E12");var subQ5=sQuery(id+"F10.wireOp",EDGE,"E30");var subQ6=sQuery(id+"F10.wireOp",EDGE,"E31");var subQ7=sQuery(id+"F10.wireOp",EDGE,"E32");var subQ8=sQuery(id+"F10.wireOp",EDGE,"E33");var subQ9=makeQuery(id+"F13.opLoft","CAP_FACE",FACE,{"disambiguationData":[OSD([makeQuery(id+"F10.imprint","IMPRINT",FACE,{"disambiguationData":[TD([[makeQuery(id+"F10.imprint","IMPRINT",EDGE,{"derivedFrom":subQ5}),1.0]])]})])],"isStart":true});var subQ10=makeQuery(id+"F16.opPattern","COPY",FACE,{"derivedFrom":makeQuery(id+"F13.opLoft","SWEPT_FACE",FACE,{"disambiguationData":[OSD([subQ1,subQ2,subQ3,subQ6,subQ7,subQ8])]}),"instanceName":"3"});Q13=makeQuery(id+"F20.boolean.opBoolean","INTERSECT",EDGE,{"derivedFrom":[makeQuery(id+"F17.opBoolean","SPLIT",FACE,{"disambiguationData":[TD([makeQuery(id+"F16.opPattern","COPY",FACE,{"derivedFrom":subQ9,"instanceName":"3"})])],"derivedFrom":subQ10}),makeQuery(id+"F20.boolean.toolComplement.opBoolean","COPY",FACE,{"derivedFrom":makeQuery(id+"F20.opExtrude","SWEPT_FACE",FACE,{"disambiguationData":[OSD([sQuery(id+"F3.wireOp",EDGE,"E3")])]})})]});}
            var Q14;
            Q14=makeQuery(id+"F16.opPattern","COPY",EDGE,{"derivedFrom":makeQuery(id+"F13.opLoft","SWEPT_EDGE",EDGE,{"disambiguationData":[OSD([sQuery(id+"F5.wireOp",EDGE,"E11"),sQuery(id+"F5.wireOp",EDGE,"E12"),sQuery(id+"F10.wireOp",EDGE,"E31"),sQuery(id+"F10.wireOp",EDGE,"E32")])]}),"instanceName":"4"});
            var Q15;
            {var subQ0=sQuery(id+"F10.wireOp",EDGE,"E30");var subQ1=sQuery(id+"F10.wireOp",EDGE,"E31");var subQ2=sQuery(id+"F10.wireOp",EDGE,"E32");var subQ3=sQuery(id+"F10.wireOp",EDGE,"E33");var subQ4=makeQuery(id+"F13.opLoft","CAP_FACE",FACE,{"disambiguationData":[OSD([makeQuery(id+"F10.imprint","IMPRINT",FACE,{"disambiguationData":[TD([[makeQuery(id+"F10.imprint","IMPRINT",EDGE,{"derivedFrom":subQ0}),1.0]])]})])],"isStart":true});var subQ6=sQuery(id+"F5.wireOp",EDGE,"E10");var subQ7=sQuery(id+"F5.wireOp",EDGE,"E11");var subQ8=sQuery(id+"F5.wireOp",EDGE,"E12");var subQ10=makeQuery(id+"F16.opPattern","COPY",FACE,{"derivedFrom":makeQuery(id+"F13.opLoft","SWEPT_FACE",FACE,{"disambiguationData":[OSD([subQ6,subQ7,subQ8,subQ1,subQ2,subQ3])]}),"instanceName":"4"});Q15=makeQuery(id+"F20.boolean.opBoolean","INTERSECT",EDGE,{"derivedFrom":[makeQuery(id+"F17.opBoolean","SPLIT",FACE,{"disambiguationData":[TD([makeQuery(id+"F16.opPattern","COPY",FACE,{"derivedFrom":subQ4,"instanceName":"4"})])],"derivedFrom":subQ10}),makeQuery(id+"F20.boolean.toolComplement.opBoolean","COPY",FACE,{"derivedFrom":makeQuery(id+"F20.opExtrude","SWEPT_FACE",FACE,{"disambiguationData":[OSD([sQuery(id+"F3.wireOp",EDGE,"E4")])]})})]});}
            var Q16;
            {var subQ0=sQuery(id+"F10.wireOp",EDGE,"E30");var subQ1=sQuery(id+"F10.wireOp",EDGE,"E31");var subQ2=sQuery(id+"F10.wireOp",EDGE,"E32");var subQ4=makeQuery(id+"F13.opLoft","CAP_FACE",FACE,{"disambiguationData":[OSD([makeQuery(id+"F10.imprint","IMPRINT",FACE,{"disambiguationData":[TD([[makeQuery(id+"F10.imprint","IMPRINT",EDGE,{"derivedFrom":subQ0}),1.0]])]})])],"isStart":true});var subQ5=sQuery(id+"F5.wireOp",EDGE,"E9");var subQ7=sQuery(id+"F5.wireOp",EDGE,"E11");var subQ8=sQuery(id+"F5.wireOp",EDGE,"E12");var subQ10=makeQuery(id+"F16.opPattern","COPY",FACE,{"derivedFrom":makeQuery(id+"F13.opLoft","SWEPT_FACE",FACE,{"disambiguationData":[OSD([subQ5,subQ7,subQ8,subQ0,subQ1,subQ2])]}),"instanceName":"5"});Q16=makeQuery(id+"F20.boolean.opBoolean","INTERSECT",EDGE,{"derivedFrom":[makeQuery(id+"F17.opBoolean","SPLIT",FACE,{"disambiguationData":[TD([makeQuery(id+"F16.opPattern","COPY",FACE,{"derivedFrom":subQ4,"instanceName":"4"})])],"derivedFrom":subQ10}),makeQuery(id+"F20.boolean.toolComplement.opBoolean","COPY",FACE,{"derivedFrom":makeQuery(id+"F20.opExtrude","SWEPT_FACE",FACE,{"disambiguationData":[OSD([sQuery(id+"F3.wireOp",EDGE,"E4")])]})})]});}
            var Q17;
            Q17=makeQuery(id+"F16.opPattern","COPY",EDGE,{"derivedFrom":makeQuery(id+"F13.opLoft","SWEPT_EDGE",EDGE,{"disambiguationData":[OSD([sQuery(id+"F5.wireOp",EDGE,"E11"),sQuery(id+"F5.wireOp",EDGE,"E12"),sQuery(id+"F10.wireOp",EDGE,"E31"),sQuery(id+"F10.wireOp",EDGE,"E32")])]}),"instanceName":"5"});
            var Q18;
            {var subQ1=sQuery(id+"F5.wireOp",EDGE,"E10");var subQ2=sQuery(id+"F5.wireOp",EDGE,"E11");var subQ3=sQuery(id+"F5.wireOp",EDGE,"E12");var subQ5=sQuery(id+"F10.wireOp",EDGE,"E32");var subQ6=sQuery(id+"F10.wireOp",EDGE,"E31");var subQ7=sQuery(id+"F10.wireOp",EDGE,"E30");var subQ9=sQuery(id+"F10.wireOp",EDGE,"E33");var subQ10=makeQuery(id+"F13.opLoft","CAP_FACE",FACE,{"disambiguationData":[OSD([makeQuery(id+"F10.imprint","IMPRINT",FACE,{"disambiguationData":[TD([[makeQuery(id+"F10.imprint","IMPRINT",EDGE,{"derivedFrom":subQ7}),1.0]])]})])],"isStart":true});var subQ11=makeQuery(id+"F16.opPattern","COPY",FACE,{"derivedFrom":makeQuery(id+"F13.opLoft","SWEPT_FACE",FACE,{"disambiguationData":[OSD([subQ1,subQ2,subQ3,subQ6,subQ5,subQ9])]}),"instanceName":"5"});Q18=makeQuery(id+"F20.boolean.opBoolean","INTERSECT",EDGE,{"derivedFrom":[makeQuery(id+"F17.opBoolean","SPLIT",FACE,{"disambiguationData":[TD([makeQuery(id+"F16.opPattern","COPY",FACE,{"derivedFrom":subQ10,"instanceName":"5"})])],"derivedFrom":subQ11}),makeQuery(id+"F20.boolean.toolComplement.opBoolean","COPY",FACE,{"derivedFrom":makeQuery(id+"F20.opExtrude","SWEPT_FACE",FACE,{"disambiguationData":[OSD([sQuery(id+"F3.wireOp",EDGE,"E4")])]})})]});}
            var Q19;
            {var subQ0=sQuery(id+"F10.wireOp",EDGE,"E32");var subQ1=sQuery(id+"F10.wireOp",EDGE,"E31");var subQ2=sQuery(id+"F10.wireOp",EDGE,"E30");var subQ3=sQuery(id+"F5.wireOp",EDGE,"E12");var subQ4=sQuery(id+"F5.wireOp",EDGE,"E11");var subQ5=sQuery(id+"F5.wireOp",EDGE,"E9");var subQ6=makeQuery(id+"F16.opPattern","COPY",FACE,{"derivedFrom":makeQuery(id+"F13.opLoft","SWEPT_FACE",FACE,{"disambiguationData":[OSD([subQ5,subQ4,subQ3,subQ2,subQ1,subQ0])]}),"instanceName":"6"});var subQ10=makeQuery(id+"F13.opLoft","CAP_FACE",FACE,{"disambiguationData":[OSD([makeQuery(id+"F10.imprint","IMPRINT",FACE,{"disambiguationData":[TD([[makeQuery(id+"F10.imprint","IMPRINT",EDGE,{"derivedFrom":subQ2}),1.0]])]})])],"isStart":true});Q19=makeQuery(id+"F20.boolean.opBoolean","INTERSECT",EDGE,{"derivedFrom":[makeQuery(id+"F17.opBoolean","SPLIT",FACE,{"disambiguationData":[TD([makeQuery(id+"F16.opPattern","COPY",FACE,{"derivedFrom":subQ10,"instanceName":"5"})])],"derivedFrom":subQ6}),makeQuery(id+"F20.boolean.toolComplement.opBoolean","COPY",FACE,{"derivedFrom":makeQuery(id+"F20.opExtrude","SWEPT_FACE",FACE,{"disambiguationData":[OSD([sQuery(id+"F3.wireOp",EDGE,"E4")])]})})]});}
            var Q20;
            {var subQ0=sQuery(id+"F10.wireOp",EDGE,"E30");var subQ1=sQuery(id+"F10.wireOp",EDGE,"E31");var subQ3=sQuery(id+"F10.wireOp",EDGE,"E33");var subQ4=makeQuery(id+"F13.opLoft","CAP_FACE",FACE,{"disambiguationData":[OSD([makeQuery(id+"F10.imprint","IMPRINT",FACE,{"disambiguationData":[TD([[makeQuery(id+"F10.imprint","IMPRINT",EDGE,{"derivedFrom":subQ0}),1.0]])]})])],"isStart":true});var subQ5=sQuery(id+"F5.wireOp",EDGE,"E12");var subQ6=sQuery(id+"F5.wireOp",EDGE,"E10");var subQ7=sQuery(id+"F5.wireOp",EDGE,"E9");var subQ8=makeQuery(id+"F16.opPattern","COPY",FACE,{"derivedFrom":makeQuery(id+"F13.opLoft","SWEPT_FACE",FACE,{"disambiguationData":[OSD([subQ7,subQ6,subQ5,subQ0,subQ1,subQ3])]}),"instanceName":"6"});Q20=makeQuery(id+"F20.boolean.opBoolean","INTERSECT",EDGE,{"derivedFrom":[makeQuery(id+"F17.opBoolean","SPLIT",FACE,{"disambiguationData":[TD([makeQuery(id+"F16.opPattern","COPY",FACE,{"derivedFrom":subQ4,"instanceName":"5"})])],"derivedFrom":subQ8}),makeQuery(id+"F20.boolean.toolComplement.opBoolean","COPY",FACE,{"derivedFrom":makeQuery(id+"F20.opExtrude","SWEPT_FACE",FACE,{"disambiguationData":[OSD([sQuery(id+"F3.wireOp",EDGE,"E4")])]})})]});}
            var Q21;
            {var subQ1=sQuery(id+"F5.wireOp",EDGE,"E10");var subQ2=sQuery(id+"F5.wireOp",EDGE,"E11");var subQ3=sQuery(id+"F5.wireOp",EDGE,"E12");var subQ5=sQuery(id+"F10.wireOp",EDGE,"E30");var subQ6=sQuery(id+"F10.wireOp",EDGE,"E31");var subQ7=sQuery(id+"F10.wireOp",EDGE,"E32");var subQ8=sQuery(id+"F10.wireOp",EDGE,"E33");var subQ9=makeQuery(id+"F13.opLoft","CAP_FACE",FACE,{"disambiguationData":[OSD([makeQuery(id+"F10.imprint","IMPRINT",FACE,{"disambiguationData":[TD([[makeQuery(id+"F10.imprint","IMPRINT",EDGE,{"derivedFrom":subQ5}),1.0]])]})])],"isStart":true});var subQ10=makeQuery(id+"F16.opPattern","COPY",FACE,{"derivedFrom":makeQuery(id+"F13.opLoft","SWEPT_FACE",FACE,{"disambiguationData":[OSD([subQ1,subQ2,subQ3,subQ6,subQ7,subQ8])]}),"instanceName":"6"});Q21=makeQuery(id+"F20.boolean.opBoolean","INTERSECT",EDGE,{"derivedFrom":[makeQuery(id+"F17.opBoolean","SPLIT",FACE,{"disambiguationData":[TD([makeQuery(id+"F16.opPattern","COPY",FACE,{"derivedFrom":subQ9,"instanceName":"6"})])],"derivedFrom":subQ10}),makeQuery(id+"F20.boolean.toolComplement.opBoolean","COPY",FACE,{"derivedFrom":makeQuery(id+"F20.opExtrude","SWEPT_FACE",FACE,{"disambiguationData":[OSD([sQuery(id+"F3.wireOp",EDGE,"E4")])]})})]});}
            var Q22;
            {var subQ0=sQuery(id+"F10.wireOp",EDGE,"E30");var subQ2=sQuery(id+"F10.wireOp",EDGE,"E32");var subQ3=sQuery(id+"F10.wireOp",EDGE,"E33");var subQ4=makeQuery(id+"F13.opLoft","CAP_FACE",FACE,{"disambiguationData":[OSD([makeQuery(id+"F10.imprint","IMPRINT",FACE,{"disambiguationData":[TD([[makeQuery(id+"F10.imprint","IMPRINT",EDGE,{"derivedFrom":subQ0}),1.0]])]})])],"isStart":true});var subQ5=sQuery(id+"F5.wireOp",EDGE,"E9");var subQ6=sQuery(id+"F5.wireOp",EDGE,"E10");var subQ7=sQuery(id+"F5.wireOp",EDGE,"E11");var subQ10=makeQuery(id+"F16.opPattern","COPY",FACE,{"derivedFrom":makeQuery(id+"F13.opLoft","SWEPT_FACE",FACE,{"disambiguationData":[OSD([subQ5,subQ6,subQ7,subQ0,subQ2,subQ3])]}),"instanceName":"6"});Q22=makeQuery(id+"F20.boolean.opBoolean","INTERSECT",EDGE,{"derivedFrom":[makeQuery(id+"F17.opBoolean","SPLIT",FACE,{"disambiguationData":[TD([makeQuery(id+"F16.opPattern","COPY",FACE,{"derivedFrom":subQ4,"instanceName":"6"})])],"derivedFrom":subQ10}),makeQuery(id+"F20.boolean.toolComplement.opBoolean","COPY",FACE,{"derivedFrom":makeQuery(id+"F20.opExtrude","SWEPT_FACE",FACE,{"disambiguationData":[OSD([sQuery(id+"F3.wireOp",EDGE,"E4")])]})})]});}
            var Q23;
            {var subQ0=sQuery(id+"F10.wireOp",EDGE,"E30");var subQ1=sQuery(id+"F10.wireOp",EDGE,"E31");var subQ3=sQuery(id+"F10.wireOp",EDGE,"E33");var subQ4=makeQuery(id+"F13.opLoft","CAP_FACE",FACE,{"disambiguationData":[OSD([makeQuery(id+"F10.imprint","IMPRINT",FACE,{"disambiguationData":[TD([[makeQuery(id+"F10.imprint","IMPRINT",EDGE,{"derivedFrom":subQ0}),1.0]])]})])],"isStart":true});var subQ5=sQuery(id+"F5.wireOp",EDGE,"E12");var subQ6=sQuery(id+"F5.wireOp",EDGE,"E10");var subQ7=sQuery(id+"F5.wireOp",EDGE,"E9");var subQ8=makeQuery(id+"F16.opPattern","COPY",FACE,{"derivedFrom":makeQuery(id+"F13.opLoft","SWEPT_FACE",FACE,{"disambiguationData":[OSD([subQ7,subQ6,subQ5,subQ0,subQ1,subQ3])]}),"instanceName":"7"});Q23=makeQuery(id+"F20.boolean.opBoolean","INTERSECT",EDGE,{"derivedFrom":[makeQuery(id+"F17.opBoolean","SPLIT",FACE,{"disambiguationData":[TD([makeQuery(id+"F16.opPattern","COPY",FACE,{"derivedFrom":subQ4,"instanceName":"6"})])],"derivedFrom":subQ8}),makeQuery(id+"F20.boolean.toolComplement.opBoolean","COPY",FACE,{"derivedFrom":makeQuery(id+"F20.opExtrude","SWEPT_FACE",FACE,{"disambiguationData":[OSD([sQuery(id+"F3.wireOp",EDGE,"E4")])]})})]});}
            var Q24;
            {var subQ0=sQuery(id+"F5.wireOp",EDGE,"E9");var subQ2=sQuery(id+"F5.wireOp",EDGE,"E11");var subQ3=sQuery(id+"F5.wireOp",EDGE,"E12");var subQ5=sQuery(id+"F10.wireOp",EDGE,"E32");var subQ6=sQuery(id+"F10.wireOp",EDGE,"E31");var subQ7=sQuery(id+"F10.wireOp",EDGE,"E30");var subQ8=makeQuery(id+"F16.opPattern","COPY",FACE,{"derivedFrom":makeQuery(id+"F13.opLoft","SWEPT_FACE",FACE,{"disambiguationData":[OSD([subQ0,subQ2,subQ3,subQ7,subQ6,subQ5])]}),"instanceName":"7"});var subQ10=makeQuery(id+"F13.opLoft","CAP_FACE",FACE,{"disambiguationData":[OSD([makeQuery(id+"F10.imprint","IMPRINT",FACE,{"disambiguationData":[TD([[makeQuery(id+"F10.imprint","IMPRINT",EDGE,{"derivedFrom":subQ7}),1.0]])]})])],"isStart":true});Q24=makeQuery(id+"F20.boolean.opBoolean","INTERSECT",EDGE,{"derivedFrom":[makeQuery(id+"F17.opBoolean","SPLIT",FACE,{"disambiguationData":[TD([makeQuery(id+"F16.opPattern","COPY",FACE,{"derivedFrom":subQ10,"instanceName":"6"})])],"derivedFrom":subQ8}),makeQuery(id+"F20.boolean.toolComplement.opBoolean","COPY",FACE,{"derivedFrom":makeQuery(id+"F20.opExtrude","SWEPT_FACE",FACE,{"disambiguationData":[OSD([sQuery(id+"F3.wireOp",EDGE,"E4")])]})})]});}
            var Q25;
            {var subQ1=sQuery(id+"F5.wireOp",EDGE,"E10");var subQ2=sQuery(id+"F5.wireOp",EDGE,"E11");var subQ3=sQuery(id+"F5.wireOp",EDGE,"E12");var subQ5=sQuery(id+"F10.wireOp",EDGE,"E33");var subQ6=sQuery(id+"F10.wireOp",EDGE,"E32");var subQ7=sQuery(id+"F10.wireOp",EDGE,"E31");var subQ8=makeQuery(id+"F16.opPattern","COPY",FACE,{"derivedFrom":makeQuery(id+"F13.opLoft","SWEPT_FACE",FACE,{"disambiguationData":[OSD([subQ1,subQ2,subQ3,subQ7,subQ6,subQ5])]}),"instanceName":"7"});var subQ9=sQuery(id+"F10.wireOp",EDGE,"E30");var subQ10=makeQuery(id+"F13.opLoft","CAP_FACE",FACE,{"disambiguationData":[OSD([makeQuery(id+"F10.imprint","IMPRINT",FACE,{"disambiguationData":[TD([[makeQuery(id+"F10.imprint","IMPRINT",EDGE,{"derivedFrom":subQ9}),1.0]])]})])],"isStart":true});Q25=makeQuery(id+"F20.boolean.opBoolean","INTERSECT",EDGE,{"derivedFrom":[makeQuery(id+"F17.opBoolean","SPLIT",FACE,{"disambiguationData":[TD([makeQuery(id+"F16.opPattern","COPY",FACE,{"derivedFrom":subQ10,"instanceName":"7"})])],"derivedFrom":subQ8}),makeQuery(id+"F20.boolean.toolComplement.opBoolean","COPY",FACE,{"derivedFrom":makeQuery(id+"F20.opExtrude","SWEPT_FACE",FACE,{"disambiguationData":[OSD([sQuery(id+"F3.wireOp",EDGE,"E4")])]})})]});}
            var Q26;
            {var subQ0=sQuery(id+"F10.wireOp",EDGE,"E30");var subQ2=sQuery(id+"F10.wireOp",EDGE,"E32");var subQ3=sQuery(id+"F10.wireOp",EDGE,"E33");var subQ4=makeQuery(id+"F13.opLoft","CAP_FACE",FACE,{"disambiguationData":[OSD([makeQuery(id+"F10.imprint","IMPRINT",FACE,{"disambiguationData":[TD([[makeQuery(id+"F10.imprint","IMPRINT",EDGE,{"derivedFrom":subQ0}),1.0]])]})])],"isStart":true});var subQ5=sQuery(id+"F5.wireOp",EDGE,"E11");var subQ6=sQuery(id+"F5.wireOp",EDGE,"E10");var subQ7=sQuery(id+"F5.wireOp",EDGE,"E9");var subQ8=makeQuery(id+"F16.opPattern","COPY",FACE,{"derivedFrom":makeQuery(id+"F13.opLoft","SWEPT_FACE",FACE,{"disambiguationData":[OSD([subQ7,subQ6,subQ5,subQ0,subQ2,subQ3])]}),"instanceName":"7"});Q26=makeQuery(id+"F20.boolean.opBoolean","INTERSECT",EDGE,{"derivedFrom":[makeQuery(id+"F17.opBoolean","SPLIT",FACE,{"disambiguationData":[TD([makeQuery(id+"F16.opPattern","COPY",FACE,{"derivedFrom":subQ4,"instanceName":"7"})])],"derivedFrom":subQ8}),makeQuery(id+"F20.boolean.toolComplement.opBoolean","COPY",FACE,{"derivedFrom":makeQuery(id+"F20.opExtrude","SWEPT_FACE",FACE,{"disambiguationData":[OSD([sQuery(id+"F3.wireOp",EDGE,"E4")])]})})]});}
            var Q27;
            {var subQ0=sQuery(id+"F10.wireOp",EDGE,"E30");var subQ1=sQuery(id+"F10.wireOp",EDGE,"E31");var subQ3=sQuery(id+"F10.wireOp",EDGE,"E33");var subQ4=makeQuery(id+"F13.opLoft","CAP_FACE",FACE,{"disambiguationData":[OSD([makeQuery(id+"F10.imprint","IMPRINT",FACE,{"disambiguationData":[TD([[makeQuery(id+"F10.imprint","IMPRINT",EDGE,{"derivedFrom":subQ0}),1.0]])]})])],"isStart":true});var subQ5=sQuery(id+"F5.wireOp",EDGE,"E12");var subQ6=sQuery(id+"F5.wireOp",EDGE,"E10");var subQ7=sQuery(id+"F5.wireOp",EDGE,"E9");var subQ8=makeQuery(id+"F16.opPattern","COPY",FACE,{"derivedFrom":makeQuery(id+"F13.opLoft","SWEPT_FACE",FACE,{"disambiguationData":[OSD([subQ7,subQ6,subQ5,subQ0,subQ1,subQ3])]}),"instanceName":"8"});Q27=makeQuery(id+"F20.boolean.opBoolean","INTERSECT",EDGE,{"derivedFrom":[makeQuery(id+"F17.opBoolean","SPLIT",FACE,{"disambiguationData":[TD([makeQuery(id+"F16.opPattern","COPY",FACE,{"derivedFrom":subQ4,"instanceName":"7"})])],"derivedFrom":subQ8}),makeQuery(id+"F20.boolean.toolComplement.opBoolean","COPY",FACE,{"derivedFrom":makeQuery(id+"F20.opExtrude","SWEPT_FACE",FACE,{"disambiguationData":[OSD([sQuery(id+"F3.wireOp",EDGE,"E4")])]})})]});}
            var Q28;
            {var subQ0=sQuery(id+"F10.wireOp",EDGE,"E30");var subQ1=sQuery(id+"F10.wireOp",EDGE,"E31");var subQ2=sQuery(id+"F10.wireOp",EDGE,"E32");var subQ3=sQuery(id+"F10.wireOp",EDGE,"E33");var subQ4=makeQuery(id+"F13.opLoft","CAP_FACE",FACE,{"disambiguationData":[OSD([makeQuery(id+"F10.imprint","IMPRINT",FACE,{"disambiguationData":[TD([[makeQuery(id+"F10.imprint","IMPRINT",EDGE,{"derivedFrom":subQ0}),1.0]])]})])],"isStart":true});var subQ6=sQuery(id+"F5.wireOp",EDGE,"E10");var subQ7=sQuery(id+"F5.wireOp",EDGE,"E11");var subQ8=sQuery(id+"F5.wireOp",EDGE,"E12");var subQ10=makeQuery(id+"F16.opPattern","COPY",FACE,{"derivedFrom":makeQuery(id+"F13.opLoft","SWEPT_FACE",FACE,{"disambiguationData":[OSD([subQ6,subQ7,subQ8,subQ1,subQ2,subQ3])]}),"instanceName":"8"});Q28=makeQuery(id+"F20.boolean.opBoolean","INTERSECT",EDGE,{"derivedFrom":[makeQuery(id+"F17.opBoolean","SPLIT",FACE,{"disambiguationData":[TD([makeQuery(id+"F16.opPattern","COPY",FACE,{"derivedFrom":subQ4,"instanceName":"8"})])],"derivedFrom":subQ10}),makeQuery(id+"F20.boolean.toolComplement.opBoolean","COPY",FACE,{"derivedFrom":makeQuery(id+"F20.opExtrude","SWEPT_FACE",FACE,{"disambiguationData":[OSD([sQuery(id+"F3.wireOp",EDGE,"E4")])]})})]});}
            var Q29;
            {var subQ0=sQuery(id+"F10.wireOp",EDGE,"E32");var subQ1=sQuery(id+"F10.wireOp",EDGE,"E31");var subQ2=sQuery(id+"F10.wireOp",EDGE,"E30");var subQ3=sQuery(id+"F5.wireOp",EDGE,"E12");var subQ4=sQuery(id+"F5.wireOp",EDGE,"E11");var subQ5=sQuery(id+"F5.wireOp",EDGE,"E9");var subQ6=makeQuery(id+"F16.opPattern","COPY",FACE,{"derivedFrom":makeQuery(id+"F13.opLoft","SWEPT_FACE",FACE,{"disambiguationData":[OSD([subQ5,subQ4,subQ3,subQ2,subQ1,subQ0])]}),"instanceName":"8"});var subQ8=makeQuery(id+"F13.opLoft","CAP_FACE",FACE,{"disambiguationData":[OSD([makeQuery(id+"F10.imprint","IMPRINT",FACE,{"disambiguationData":[TD([[makeQuery(id+"F10.imprint","IMPRINT",EDGE,{"derivedFrom":subQ2}),1.0]])]})])],"isStart":true});Q29=makeQuery(id+"F20.boolean.opBoolean","INTERSECT",EDGE,{"derivedFrom":[makeQuery(id+"F17.opBoolean","SPLIT",FACE,{"disambiguationData":[TD([makeQuery(id+"F16.opPattern","COPY",FACE,{"derivedFrom":subQ8,"instanceName":"7"})])],"derivedFrom":subQ6}),makeQuery(id+"F20.boolean.toolComplement.opBoolean","COPY",FACE,{"derivedFrom":makeQuery(id+"F20.opExtrude","SWEPT_FACE",FACE,{"disambiguationData":[OSD([sQuery(id+"F3.wireOp",EDGE,"E4")])]})})]});}
            var Q30;
            {var subQ0=sQuery(id+"F10.wireOp",EDGE,"E30");var subQ1=sQuery(id+"F10.wireOp",EDGE,"E31");var subQ2=sQuery(id+"F10.wireOp",EDGE,"E32");var subQ4=makeQuery(id+"F13.opLoft","CAP_FACE",FACE,{"disambiguationData":[OSD([makeQuery(id+"F10.imprint","IMPRINT",FACE,{"disambiguationData":[TD([[makeQuery(id+"F10.imprint","IMPRINT",EDGE,{"derivedFrom":subQ0}),1.0]])]})])],"isStart":true});var subQ5=sQuery(id+"F5.wireOp",EDGE,"E9");var subQ7=sQuery(id+"F5.wireOp",EDGE,"E11");var subQ8=sQuery(id+"F5.wireOp",EDGE,"E12");var subQ10=makeQuery(id+"F16.opPattern","COPY",FACE,{"derivedFrom":makeQuery(id+"F13.opLoft","SWEPT_FACE",FACE,{"disambiguationData":[OSD([subQ5,subQ7,subQ8,subQ0,subQ1,subQ2])]}),"instanceName":"9"});Q30=makeQuery(id+"F20.boolean.opBoolean","INTERSECT",EDGE,{"derivedFrom":[makeQuery(id+"F17.opBoolean","SPLIT",FACE,{"disambiguationData":[TD([makeQuery(id+"F16.opPattern","COPY",FACE,{"derivedFrom":subQ4,"instanceName":"8"})])],"derivedFrom":subQ10}),makeQuery(id+"F20.boolean.toolComplement.opBoolean","COPY",FACE,{"derivedFrom":makeQuery(id+"F20.opExtrude","SWEPT_FACE",FACE,{"disambiguationData":[OSD([sQuery(id+"F3.wireOp",EDGE,"E4")])]})})]});}
            var Q31;
            {var subQ0=sQuery(id+"F10.wireOp",EDGE,"E30");var subQ1=sQuery(id+"F10.wireOp",EDGE,"E31");var subQ3=sQuery(id+"F10.wireOp",EDGE,"E33");var subQ4=makeQuery(id+"F13.opLoft","CAP_FACE",FACE,{"disambiguationData":[OSD([makeQuery(id+"F10.imprint","IMPRINT",FACE,{"disambiguationData":[TD([[makeQuery(id+"F10.imprint","IMPRINT",EDGE,{"derivedFrom":subQ0}),1.0]])]})])],"isStart":true});var subQ6=sQuery(id+"F5.wireOp",EDGE,"E10");var subQ7=sQuery(id+"F5.wireOp",EDGE,"E9");var subQ9=sQuery(id+"F5.wireOp",EDGE,"E12");var subQ11=makeQuery(id+"F16.opPattern","COPY",FACE,{"derivedFrom":makeQuery(id+"F13.opLoft","SWEPT_FACE",FACE,{"disambiguationData":[OSD([subQ7,subQ6,subQ9,subQ0,subQ1,subQ3])]}),"instanceName":"9"});Q31=makeQuery(id+"F20.boolean.opBoolean","INTERSECT",EDGE,{"derivedFrom":[makeQuery(id+"F17.opBoolean","SPLIT",FACE,{"disambiguationData":[TD([makeQuery(id+"F16.opPattern","COPY",FACE,{"derivedFrom":subQ4,"instanceName":"8"})])],"derivedFrom":subQ11}),makeQuery(id+"F20.boolean.toolComplement.opBoolean","COPY",FACE,{"derivedFrom":makeQuery(id+"F20.opExtrude","SWEPT_FACE",FACE,{"disambiguationData":[OSD([sQuery(id+"F3.wireOp",EDGE,"E4")])]})})]});}
            var Q32;
            {var subQ0=sQuery(id+"F10.wireOp",EDGE,"E30");var subQ2=sQuery(id+"F10.wireOp",EDGE,"E32");var subQ3=sQuery(id+"F10.wireOp",EDGE,"E33");var subQ4=makeQuery(id+"F13.opLoft","CAP_FACE",FACE,{"disambiguationData":[OSD([makeQuery(id+"F10.imprint","IMPRINT",FACE,{"disambiguationData":[TD([[makeQuery(id+"F10.imprint","IMPRINT",EDGE,{"derivedFrom":subQ0}),1.0]])]})])],"isStart":true});var subQ5=sQuery(id+"F5.wireOp",EDGE,"E11");var subQ6=sQuery(id+"F5.wireOp",EDGE,"E10");var subQ7=sQuery(id+"F5.wireOp",EDGE,"E9");var subQ8=makeQuery(id+"F16.opPattern","COPY",FACE,{"derivedFrom":makeQuery(id+"F13.opLoft","SWEPT_FACE",FACE,{"disambiguationData":[OSD([subQ7,subQ6,subQ5,subQ0,subQ2,subQ3])]}),"instanceName":"8"});Q32=makeQuery(id+"F20.boolean.opBoolean","INTERSECT",EDGE,{"derivedFrom":[makeQuery(id+"F17.opBoolean","SPLIT",FACE,{"disambiguationData":[TD([makeQuery(id+"F16.opPattern","COPY",FACE,{"derivedFrom":subQ4,"instanceName":"8"})])],"derivedFrom":subQ8}),makeQuery(id+"F20.boolean.toolComplement.opBoolean","COPY",FACE,{"derivedFrom":makeQuery(id+"F20.opExtrude","SWEPT_FACE",FACE,{"disambiguationData":[OSD([sQuery(id+"F3.wireOp",EDGE,"E4")])]})})]});}
            var Q33;
            {var subQ0=sQuery(id+"F10.wireOp",EDGE,"E30");var subQ1=sQuery(id+"F10.wireOp",EDGE,"E31");var subQ2=sQuery(id+"F10.wireOp",EDGE,"E32");var subQ3=sQuery(id+"F10.wireOp",EDGE,"E33");var subQ4=makeQuery(id+"F13.opLoft","CAP_FACE",FACE,{"disambiguationData":[OSD([makeQuery(id+"F10.imprint","IMPRINT",FACE,{"disambiguationData":[TD([[makeQuery(id+"F10.imprint","IMPRINT",EDGE,{"derivedFrom":subQ0}),1.0]])]})])],"isStart":true});var subQ6=sQuery(id+"F5.wireOp",EDGE,"E10");var subQ7=sQuery(id+"F5.wireOp",EDGE,"E11");var subQ8=sQuery(id+"F5.wireOp",EDGE,"E12");var subQ11=makeQuery(id+"F16.opPattern","COPY",FACE,{"derivedFrom":makeQuery(id+"F13.opLoft","SWEPT_FACE",FACE,{"disambiguationData":[OSD([subQ6,subQ7,subQ8,subQ1,subQ2,subQ3])]}),"instanceName":"9"});Q33=makeQuery(id+"F20.boolean.opBoolean","INTERSECT",EDGE,{"derivedFrom":[makeQuery(id+"F17.opBoolean","SPLIT",FACE,{"disambiguationData":[TD([makeQuery(id+"F16.opPattern","COPY",FACE,{"derivedFrom":subQ4,"instanceName":"9"})])],"derivedFrom":subQ11}),makeQuery(id+"F20.boolean.toolComplement.opBoolean","COPY",FACE,{"derivedFrom":makeQuery(id+"F20.opExtrude","SWEPT_FACE",FACE,{"disambiguationData":[OSD([sQuery(id+"F3.wireOp",EDGE,"E4")])]})})]});}
            var Q34;
            {var subQ0=sQuery(id+"F10.wireOp",EDGE,"E30");var subQ2=sQuery(id+"F10.wireOp",EDGE,"E32");var subQ3=sQuery(id+"F10.wireOp",EDGE,"E33");var subQ4=makeQuery(id+"F13.opLoft","CAP_FACE",FACE,{"disambiguationData":[OSD([makeQuery(id+"F10.imprint","IMPRINT",FACE,{"disambiguationData":[TD([[makeQuery(id+"F10.imprint","IMPRINT",EDGE,{"derivedFrom":subQ0}),1.0]])]})])],"isStart":true});var subQ5=sQuery(id+"F5.wireOp",EDGE,"E11");var subQ6=sQuery(id+"F5.wireOp",EDGE,"E10");var subQ7=sQuery(id+"F5.wireOp",EDGE,"E9");var subQ8=makeQuery(id+"F16.opPattern","COPY",FACE,{"derivedFrom":makeQuery(id+"F13.opLoft","SWEPT_FACE",FACE,{"disambiguationData":[OSD([subQ7,subQ6,subQ5,subQ0,subQ2,subQ3])]}),"instanceName":"9"});Q34=makeQuery(id+"F20.boolean.opBoolean","INTERSECT",EDGE,{"derivedFrom":[makeQuery(id+"F17.opBoolean","SPLIT",FACE,{"disambiguationData":[TD([makeQuery(id+"F16.opPattern","COPY",FACE,{"derivedFrom":subQ4,"instanceName":"9"})])],"derivedFrom":subQ8}),makeQuery(id+"F20.boolean.toolComplement.opBoolean","COPY",FACE,{"derivedFrom":makeQuery(id+"F20.opExtrude","SWEPT_FACE",FACE,{"disambiguationData":[OSD([sQuery(id+"F3.wireOp",EDGE,"E4")])]})})]});}
            var Q35;
            {var subQ0=sQuery(id+"F10.wireOp",EDGE,"E33");var subQ1=sQuery(id+"F10.wireOp",EDGE,"E31");var subQ2=sQuery(id+"F10.wireOp",EDGE,"E30");var subQ3=sQuery(id+"F5.wireOp",EDGE,"E12");var subQ4=sQuery(id+"F5.wireOp",EDGE,"E10");var subQ5=sQuery(id+"F5.wireOp",EDGE,"E9");var subQ6=makeQuery(id+"F16.opPattern","COPY",FACE,{"derivedFrom":makeQuery(id+"F13.opLoft","SWEPT_FACE",FACE,{"disambiguationData":[OSD([subQ5,subQ4,subQ3,subQ2,subQ1,subQ0])]}),"instanceName":"10"});var subQ8=makeQuery(id+"F13.opLoft","CAP_FACE",FACE,{"disambiguationData":[OSD([makeQuery(id+"F10.imprint","IMPRINT",FACE,{"disambiguationData":[TD([[makeQuery(id+"F10.imprint","IMPRINT",EDGE,{"derivedFrom":subQ2}),1.0]])]})])],"isStart":true});Q35=makeQuery(id+"F20.boolean.opBoolean","INTERSECT",EDGE,{"derivedFrom":[makeQuery(id+"F17.opBoolean","SPLIT",FACE,{"disambiguationData":[TD([makeQuery(id+"F16.opPattern","COPY",FACE,{"derivedFrom":subQ8,"instanceName":"9"})])],"derivedFrom":subQ6}),makeQuery(id+"F20.boolean.toolComplement.opBoolean","COPY",FACE,{"derivedFrom":makeQuery(id+"F20.opExtrude","SWEPT_FACE",FACE,{"disambiguationData":[OSD([sQuery(id+"F3.wireOp",EDGE,"E4")])]})})]});}
            var Q36;
            {var subQ0=sQuery(id+"F10.wireOp",EDGE,"E32");var subQ1=sQuery(id+"F10.wireOp",EDGE,"E31");var subQ2=sQuery(id+"F10.wireOp",EDGE,"E30");var subQ3=sQuery(id+"F5.wireOp",EDGE,"E12");var subQ4=sQuery(id+"F5.wireOp",EDGE,"E11");var subQ5=sQuery(id+"F5.wireOp",EDGE,"E9");var subQ6=makeQuery(id+"F16.opPattern","COPY",FACE,{"derivedFrom":makeQuery(id+"F13.opLoft","SWEPT_FACE",FACE,{"disambiguationData":[OSD([subQ5,subQ4,subQ3,subQ2,subQ1,subQ0])]}),"instanceName":"10"});var subQ10=makeQuery(id+"F13.opLoft","CAP_FACE",FACE,{"disambiguationData":[OSD([makeQuery(id+"F10.imprint","IMPRINT",FACE,{"disambiguationData":[TD([[makeQuery(id+"F10.imprint","IMPRINT",EDGE,{"derivedFrom":subQ2}),1.0]])]})])],"isStart":true});Q36=makeQuery(id+"F20.boolean.opBoolean","INTERSECT",EDGE,{"derivedFrom":[makeQuery(id+"F17.opBoolean","SPLIT",FACE,{"disambiguationData":[TD([makeQuery(id+"F16.opPattern","COPY",FACE,{"derivedFrom":subQ10,"instanceName":"9"})])],"derivedFrom":subQ6}),makeQuery(id+"F20.boolean.toolComplement.opBoolean","COPY",FACE,{"derivedFrom":makeQuery(id+"F20.opExtrude","SWEPT_FACE",FACE,{"disambiguationData":[OSD([sQuery(id+"F3.wireOp",EDGE,"E4")])]})})]});}
            var Q37;
            {var subQ1=sQuery(id+"F5.wireOp",EDGE,"E10");var subQ2=sQuery(id+"F5.wireOp",EDGE,"E11");var subQ3=sQuery(id+"F5.wireOp",EDGE,"E12");var subQ5=sQuery(id+"F10.wireOp",EDGE,"E30");var subQ6=sQuery(id+"F10.wireOp",EDGE,"E31");var subQ7=sQuery(id+"F10.wireOp",EDGE,"E32");var subQ8=sQuery(id+"F10.wireOp",EDGE,"E33");var subQ9=makeQuery(id+"F13.opLoft","CAP_FACE",FACE,{"disambiguationData":[OSD([makeQuery(id+"F10.imprint","IMPRINT",FACE,{"disambiguationData":[TD([[makeQuery(id+"F10.imprint","IMPRINT",EDGE,{"derivedFrom":subQ5}),1.0]])]})])],"isStart":true});var subQ10=makeQuery(id+"F16.opPattern","COPY",FACE,{"derivedFrom":makeQuery(id+"F13.opLoft","SWEPT_FACE",FACE,{"disambiguationData":[OSD([subQ1,subQ2,subQ3,subQ6,subQ7,subQ8])]}),"instanceName":"10"});Q37=makeQuery(id+"F20.boolean.opBoolean","INTERSECT",EDGE,{"derivedFrom":[makeQuery(id+"F17.opBoolean","SPLIT",FACE,{"disambiguationData":[TD([makeQuery(id+"F16.opPattern","COPY",FACE,{"derivedFrom":subQ9,"instanceName":"10"})])],"derivedFrom":subQ10}),makeQuery(id+"F20.boolean.toolComplement.opBoolean","COPY",FACE,{"derivedFrom":makeQuery(id+"F20.opExtrude","SWEPT_FACE",FACE,{"disambiguationData":[OSD([sQuery(id+"F3.wireOp",EDGE,"E4")])]})})]});}
            var Q38;
            {var subQ0=sQuery(id+"F10.wireOp",EDGE,"E30");var subQ2=sQuery(id+"F10.wireOp",EDGE,"E32");var subQ3=sQuery(id+"F10.wireOp",EDGE,"E33");var subQ4=makeQuery(id+"F13.opLoft","CAP_FACE",FACE,{"disambiguationData":[OSD([makeQuery(id+"F10.imprint","IMPRINT",FACE,{"disambiguationData":[TD([[makeQuery(id+"F10.imprint","IMPRINT",EDGE,{"derivedFrom":subQ0}),1.0]])]})])],"isStart":true});var subQ5=sQuery(id+"F5.wireOp",EDGE,"E9");var subQ6=sQuery(id+"F5.wireOp",EDGE,"E10");var subQ7=sQuery(id+"F5.wireOp",EDGE,"E11");var subQ10=makeQuery(id+"F16.opPattern","COPY",FACE,{"derivedFrom":makeQuery(id+"F13.opLoft","SWEPT_FACE",FACE,{"disambiguationData":[OSD([subQ5,subQ6,subQ7,subQ0,subQ2,subQ3])]}),"instanceName":"10"});Q38=makeQuery(id+"F20.boolean.opBoolean","INTERSECT",EDGE,{"derivedFrom":[makeQuery(id+"F17.opBoolean","SPLIT",FACE,{"disambiguationData":[TD([makeQuery(id+"F16.opPattern","COPY",FACE,{"derivedFrom":subQ4,"instanceName":"10"})])],"derivedFrom":subQ10}),makeQuery(id+"F20.boolean.toolComplement.opBoolean","COPY",FACE,{"derivedFrom":makeQuery(id+"F20.opExtrude","SWEPT_FACE",FACE,{"disambiguationData":[OSD([sQuery(id+"F3.wireOp",EDGE,"E4")])]})})]});}
            var Q39;
            {var subQ0=sQuery(id+"F10.wireOp",EDGE,"E32");var subQ1=sQuery(id+"F10.wireOp",EDGE,"E31");var subQ2=sQuery(id+"F10.wireOp",EDGE,"E30");var subQ3=sQuery(id+"F5.wireOp",EDGE,"E12");var subQ4=sQuery(id+"F5.wireOp",EDGE,"E11");var subQ5=sQuery(id+"F5.wireOp",EDGE,"E9");var subQ6=makeQuery(id+"F16.opPattern","COPY",FACE,{"derivedFrom":makeQuery(id+"F13.opLoft","SWEPT_FACE",FACE,{"disambiguationData":[OSD([subQ5,subQ4,subQ3,subQ2,subQ1,subQ0])]}),"instanceName":"11"});var subQ10=makeQuery(id+"F13.opLoft","CAP_FACE",FACE,{"disambiguationData":[OSD([makeQuery(id+"F10.imprint","IMPRINT",FACE,{"disambiguationData":[TD([[makeQuery(id+"F10.imprint","IMPRINT",EDGE,{"derivedFrom":subQ2}),1.0]])]})])],"isStart":true});Q39=makeQuery(id+"F20.boolean.opBoolean","INTERSECT",EDGE,{"derivedFrom":[makeQuery(id+"F17.opBoolean","SPLIT",FACE,{"disambiguationData":[TD([makeQuery(id+"F16.opPattern","COPY",FACE,{"derivedFrom":subQ10,"instanceName":"10"})])],"derivedFrom":subQ6}),makeQuery(id+"F20.boolean.toolComplement.opBoolean","COPY",FACE,{"derivedFrom":makeQuery(id+"F20.opExtrude","SWEPT_FACE",FACE,{"disambiguationData":[OSD([sQuery(id+"F3.wireOp",EDGE,"E4")])]})})]});}
            var Q40;
            {var subQ0=sQuery(id+"F10.wireOp",EDGE,"E30");var subQ1=sQuery(id+"F10.wireOp",EDGE,"E31");var subQ3=sQuery(id+"F10.wireOp",EDGE,"E33");var subQ4=makeQuery(id+"F13.opLoft","CAP_FACE",FACE,{"disambiguationData":[OSD([makeQuery(id+"F10.imprint","IMPRINT",FACE,{"disambiguationData":[TD([[makeQuery(id+"F10.imprint","IMPRINT",EDGE,{"derivedFrom":subQ0}),1.0]])]})])],"isStart":true});var subQ5=sQuery(id+"F5.wireOp",EDGE,"E9");var subQ6=sQuery(id+"F5.wireOp",EDGE,"E10");var subQ8=sQuery(id+"F5.wireOp",EDGE,"E12");var subQ10=makeQuery(id+"F16.opPattern","COPY",FACE,{"derivedFrom":makeQuery(id+"F13.opLoft","SWEPT_FACE",FACE,{"disambiguationData":[OSD([subQ5,subQ6,subQ8,subQ0,subQ1,subQ3])]}),"instanceName":"11"});Q40=makeQuery(id+"F20.boolean.opBoolean","INTERSECT",EDGE,{"derivedFrom":[makeQuery(id+"F17.opBoolean","SPLIT",FACE,{"disambiguationData":[TD([makeQuery(id+"F16.opPattern","COPY",FACE,{"derivedFrom":subQ4,"instanceName":"10"})])],"derivedFrom":subQ10}),makeQuery(id+"F20.boolean.toolComplement.opBoolean","COPY",FACE,{"derivedFrom":makeQuery(id+"F20.opExtrude","SWEPT_FACE",FACE,{"disambiguationData":[OSD([sQuery(id+"F3.wireOp",EDGE,"E4")])]})})]});}
            var Q41;
            {var subQ0=sQuery(id+"F10.wireOp",EDGE,"E30");var subQ1=sQuery(id+"F10.wireOp",EDGE,"E31");var subQ2=sQuery(id+"F10.wireOp",EDGE,"E32");var subQ3=sQuery(id+"F10.wireOp",EDGE,"E33");var subQ4=makeQuery(id+"F13.opLoft","CAP_FACE",FACE,{"disambiguationData":[OSD([makeQuery(id+"F10.imprint","IMPRINT",FACE,{"disambiguationData":[TD([[makeQuery(id+"F10.imprint","IMPRINT",EDGE,{"derivedFrom":subQ0}),1.0]])]})])],"isStart":true});var subQ6=sQuery(id+"F5.wireOp",EDGE,"E10");var subQ7=sQuery(id+"F5.wireOp",EDGE,"E11");var subQ8=sQuery(id+"F5.wireOp",EDGE,"E12");var subQ10=makeQuery(id+"F16.opPattern","COPY",FACE,{"derivedFrom":makeQuery(id+"F13.opLoft","SWEPT_FACE",FACE,{"disambiguationData":[OSD([subQ6,subQ7,subQ8,subQ1,subQ2,subQ3])]}),"instanceName":"11"});Q41=makeQuery(id+"F20.boolean.opBoolean","INTERSECT",EDGE,{"derivedFrom":[makeQuery(id+"F17.opBoolean","SPLIT",FACE,{"disambiguationData":[TD([makeQuery(id+"F16.opPattern","COPY",FACE,{"derivedFrom":subQ4,"instanceName":"11"})])],"derivedFrom":subQ10}),makeQuery(id+"F20.boolean.toolComplement.opBoolean","COPY",FACE,{"derivedFrom":makeQuery(id+"F20.opExtrude","SWEPT_FACE",FACE,{"disambiguationData":[OSD([sQuery(id+"F3.wireOp",EDGE,"E4")])]})})]});}
            var Q42;
            {var subQ0=sQuery(id+"F5.wireOp",EDGE,"E9");var subQ1=sQuery(id+"F5.wireOp",EDGE,"E10");var subQ2=sQuery(id+"F5.wireOp",EDGE,"E11");var subQ5=sQuery(id+"F10.wireOp",EDGE,"E33");var subQ6=sQuery(id+"F10.wireOp",EDGE,"E32");var subQ7=sQuery(id+"F10.wireOp",EDGE,"E30");var subQ8=makeQuery(id+"F16.opPattern","COPY",FACE,{"derivedFrom":makeQuery(id+"F13.opLoft","SWEPT_FACE",FACE,{"disambiguationData":[OSD([subQ0,subQ1,subQ2,subQ7,subQ6,subQ5])]}),"instanceName":"11"});var subQ10=makeQuery(id+"F13.opLoft","CAP_FACE",FACE,{"disambiguationData":[OSD([makeQuery(id+"F10.imprint","IMPRINT",FACE,{"disambiguationData":[TD([[makeQuery(id+"F10.imprint","IMPRINT",EDGE,{"derivedFrom":subQ7}),1.0]])]})])],"isStart":true});Q42=makeQuery(id+"F20.boolean.opBoolean","INTERSECT",EDGE,{"derivedFrom":[makeQuery(id+"F17.opBoolean","SPLIT",FACE,{"disambiguationData":[TD([makeQuery(id+"F16.opPattern","COPY",FACE,{"derivedFrom":subQ10,"instanceName":"11"})])],"derivedFrom":subQ8}),makeQuery(id+"F20.boolean.toolComplement.opBoolean","COPY",FACE,{"derivedFrom":makeQuery(id+"F20.opExtrude","SWEPT_FACE",FACE,{"disambiguationData":[OSD([sQuery(id+"F3.wireOp",EDGE,"E4")])]})})]});}
            var Q43;
            {var subQ0=sQuery(id+"F10.wireOp",EDGE,"E32");var subQ1=sQuery(id+"F10.wireOp",EDGE,"E31");var subQ2=sQuery(id+"F10.wireOp",EDGE,"E30");var subQ3=sQuery(id+"F5.wireOp",EDGE,"E12");var subQ4=sQuery(id+"F5.wireOp",EDGE,"E11");var subQ5=sQuery(id+"F5.wireOp",EDGE,"E9");var subQ6=makeQuery(id+"F16.opPattern","COPY",FACE,{"derivedFrom":makeQuery(id+"F13.opLoft","SWEPT_FACE",FACE,{"disambiguationData":[OSD([subQ5,subQ4,subQ3,subQ2,subQ1,subQ0])]}),"instanceName":"12"});var subQ8=makeQuery(id+"F13.opLoft","CAP_FACE",FACE,{"disambiguationData":[OSD([makeQuery(id+"F10.imprint","IMPRINT",FACE,{"disambiguationData":[TD([[makeQuery(id+"F10.imprint","IMPRINT",EDGE,{"derivedFrom":subQ2}),1.0]])]})])],"isStart":true});Q43=makeQuery(id+"F20.boolean.opBoolean","INTERSECT",EDGE,{"derivedFrom":[makeQuery(id+"F17.opBoolean","SPLIT",FACE,{"disambiguationData":[TD([makeQuery(id+"F16.opPattern","COPY",FACE,{"derivedFrom":subQ8,"instanceName":"11"})])],"derivedFrom":subQ6}),makeQuery(id+"F20.boolean.toolComplement.opBoolean","COPY",FACE,{"derivedFrom":makeQuery(id+"F20.opExtrude","SWEPT_FACE",FACE,{"disambiguationData":[OSD([sQuery(id+"F3.wireOp",EDGE,"E4")])]})})]});}
            var Q44;
            {var subQ0=sQuery(id+"F10.wireOp",EDGE,"E30");var subQ1=sQuery(id+"F10.wireOp",EDGE,"E31");var subQ3=sQuery(id+"F10.wireOp",EDGE,"E33");var subQ4=makeQuery(id+"F13.opLoft","CAP_FACE",FACE,{"disambiguationData":[OSD([makeQuery(id+"F10.imprint","IMPRINT",FACE,{"disambiguationData":[TD([[makeQuery(id+"F10.imprint","IMPRINT",EDGE,{"derivedFrom":subQ0}),1.0]])]})])],"isStart":true});var subQ5=sQuery(id+"F5.wireOp",EDGE,"E12");var subQ6=sQuery(id+"F5.wireOp",EDGE,"E10");var subQ7=sQuery(id+"F5.wireOp",EDGE,"E9");var subQ8=makeQuery(id+"F16.opPattern","COPY",FACE,{"derivedFrom":makeQuery(id+"F13.opLoft","SWEPT_FACE",FACE,{"disambiguationData":[OSD([subQ7,subQ6,subQ5,subQ0,subQ1,subQ3])]}),"instanceName":"12"});Q44=makeQuery(id+"F20.boolean.opBoolean","INTERSECT",EDGE,{"derivedFrom":[makeQuery(id+"F17.opBoolean","SPLIT",FACE,{"disambiguationData":[TD([makeQuery(id+"F16.opPattern","COPY",FACE,{"derivedFrom":subQ4,"instanceName":"11"})])],"derivedFrom":subQ8}),makeQuery(id+"F20.boolean.toolComplement.opBoolean","COPY",FACE,{"derivedFrom":makeQuery(id+"F20.opExtrude","SWEPT_FACE",FACE,{"disambiguationData":[OSD([sQuery(id+"F3.wireOp",EDGE,"E4")])]})})]});}
            var Q45;
            {var subQ1=sQuery(id+"F5.wireOp",EDGE,"E10");var subQ2=sQuery(id+"F5.wireOp",EDGE,"E11");var subQ3=sQuery(id+"F5.wireOp",EDGE,"E12");var subQ5=sQuery(id+"F10.wireOp",EDGE,"E30");var subQ6=sQuery(id+"F10.wireOp",EDGE,"E31");var subQ7=sQuery(id+"F10.wireOp",EDGE,"E32");var subQ8=sQuery(id+"F10.wireOp",EDGE,"E33");var subQ9=makeQuery(id+"F13.opLoft","CAP_FACE",FACE,{"disambiguationData":[OSD([makeQuery(id+"F10.imprint","IMPRINT",FACE,{"disambiguationData":[TD([[makeQuery(id+"F10.imprint","IMPRINT",EDGE,{"derivedFrom":subQ5}),1.0]])]})])],"isStart":true});var subQ10=makeQuery(id+"F16.opPattern","COPY",FACE,{"derivedFrom":makeQuery(id+"F13.opLoft","SWEPT_FACE",FACE,{"disambiguationData":[OSD([subQ1,subQ2,subQ3,subQ6,subQ7,subQ8])]}),"instanceName":"12"});Q45=makeQuery(id+"F20.boolean.opBoolean","INTERSECT",EDGE,{"derivedFrom":[makeQuery(id+"F17.opBoolean","SPLIT",FACE,{"disambiguationData":[TD([makeQuery(id+"F16.opPattern","COPY",FACE,{"derivedFrom":subQ9,"instanceName":"12"})])],"derivedFrom":subQ10}),makeQuery(id+"F20.boolean.toolComplement.opBoolean","COPY",FACE,{"derivedFrom":makeQuery(id+"F20.opExtrude","SWEPT_FACE",FACE,{"disambiguationData":[OSD([sQuery(id+"F3.wireOp",EDGE,"E4")])]})})]});}
            var Q46;
            {var subQ0=sQuery(id+"F10.wireOp",EDGE,"E30");var subQ2=sQuery(id+"F10.wireOp",EDGE,"E32");var subQ3=sQuery(id+"F10.wireOp",EDGE,"E33");var subQ4=makeQuery(id+"F13.opLoft","CAP_FACE",FACE,{"disambiguationData":[OSD([makeQuery(id+"F10.imprint","IMPRINT",FACE,{"disambiguationData":[TD([[makeQuery(id+"F10.imprint","IMPRINT",EDGE,{"derivedFrom":subQ0}),1.0]])]})])],"isStart":true});var subQ5=sQuery(id+"F5.wireOp",EDGE,"E9");var subQ6=sQuery(id+"F5.wireOp",EDGE,"E10");var subQ7=sQuery(id+"F5.wireOp",EDGE,"E11");var subQ10=makeQuery(id+"F16.opPattern","COPY",FACE,{"derivedFrom":makeQuery(id+"F13.opLoft","SWEPT_FACE",FACE,{"disambiguationData":[OSD([subQ5,subQ6,subQ7,subQ0,subQ2,subQ3])]}),"instanceName":"12"});Q46=makeQuery(id+"F20.boolean.opBoolean","INTERSECT",EDGE,{"derivedFrom":[makeQuery(id+"F17.opBoolean","SPLIT",FACE,{"disambiguationData":[TD([makeQuery(id+"F16.opPattern","COPY",FACE,{"derivedFrom":subQ4,"instanceName":"12"})])],"derivedFrom":subQ10}),makeQuery(id+"F20.boolean.toolComplement.opBoolean","COPY",FACE,{"derivedFrom":makeQuery(id+"F20.opExtrude","SWEPT_FACE",FACE,{"disambiguationData":[OSD([sQuery(id+"F3.wireOp",EDGE,"E4")])]})})]});}
            var Q47;
            {var subQ0=sQuery(id+"F10.wireOp",EDGE,"E32");var subQ1=sQuery(id+"F10.wireOp",EDGE,"E31");var subQ2=sQuery(id+"F10.wireOp",EDGE,"E30");var subQ3=sQuery(id+"F5.wireOp",EDGE,"E12");var subQ4=sQuery(id+"F5.wireOp",EDGE,"E11");var subQ5=sQuery(id+"F5.wireOp",EDGE,"E9");var subQ6=makeQuery(id+"F16.opPattern","COPY",FACE,{"derivedFrom":makeQuery(id+"F13.opLoft","SWEPT_FACE",FACE,{"disambiguationData":[OSD([subQ5,subQ4,subQ3,subQ2,subQ1,subQ0])]}),"instanceName":"13"});var subQ10=makeQuery(id+"F13.opLoft","CAP_FACE",FACE,{"disambiguationData":[OSD([makeQuery(id+"F10.imprint","IMPRINT",FACE,{"disambiguationData":[TD([[makeQuery(id+"F10.imprint","IMPRINT",EDGE,{"derivedFrom":subQ2}),1.0]])]})])],"isStart":true});Q47=makeQuery(id+"F20.boolean.opBoolean","INTERSECT",EDGE,{"derivedFrom":[makeQuery(id+"F17.opBoolean","SPLIT",FACE,{"disambiguationData":[TD([makeQuery(id+"F16.opPattern","COPY",FACE,{"derivedFrom":subQ10,"instanceName":"12"})])],"derivedFrom":subQ6}),makeQuery(id+"F20.boolean.toolComplement.opBoolean","COPY",FACE,{"derivedFrom":makeQuery(id+"F20.opExtrude","SWEPT_FACE",FACE,{"disambiguationData":[OSD([sQuery(id+"F3.wireOp",EDGE,"E4")])]})})]});}
            var Q48;
            {var subQ0=sQuery(id+"F10.wireOp",EDGE,"E33");var subQ1=sQuery(id+"F10.wireOp",EDGE,"E31");var subQ2=sQuery(id+"F10.wireOp",EDGE,"E30");var subQ3=sQuery(id+"F5.wireOp",EDGE,"E12");var subQ4=sQuery(id+"F5.wireOp",EDGE,"E10");var subQ5=sQuery(id+"F5.wireOp",EDGE,"E9");var subQ6=makeQuery(id+"F16.opPattern","COPY",FACE,{"derivedFrom":makeQuery(id+"F13.opLoft","SWEPT_FACE",FACE,{"disambiguationData":[OSD([subQ5,subQ4,subQ3,subQ2,subQ1,subQ0])]}),"instanceName":"13"});var subQ8=makeQuery(id+"F13.opLoft","CAP_FACE",FACE,{"disambiguationData":[OSD([makeQuery(id+"F10.imprint","IMPRINT",FACE,{"disambiguationData":[TD([[makeQuery(id+"F10.imprint","IMPRINT",EDGE,{"derivedFrom":subQ2}),1.0]])]})])],"isStart":true});Q48=makeQuery(id+"F20.boolean.opBoolean","INTERSECT",EDGE,{"derivedFrom":[makeQuery(id+"F17.opBoolean","SPLIT",FACE,{"disambiguationData":[TD([makeQuery(id+"F16.opPattern","COPY",FACE,{"derivedFrom":subQ8,"instanceName":"12"})])],"derivedFrom":subQ6}),makeQuery(id+"F20.boolean.toolComplement.opBoolean","COPY",FACE,{"derivedFrom":makeQuery(id+"F20.opExtrude","SWEPT_FACE",FACE,{"disambiguationData":[OSD([sQuery(id+"F3.wireOp",EDGE,"E4")])]})})]});}
            var Q49;
            {var subQ0=sQuery(id+"F10.wireOp",EDGE,"E30");var subQ1=sQuery(id+"F10.wireOp",EDGE,"E31");var subQ2=sQuery(id+"F10.wireOp",EDGE,"E32");var subQ3=sQuery(id+"F10.wireOp",EDGE,"E33");var subQ4=makeQuery(id+"F13.opLoft","CAP_FACE",FACE,{"disambiguationData":[OSD([makeQuery(id+"F10.imprint","IMPRINT",FACE,{"disambiguationData":[TD([[makeQuery(id+"F10.imprint","IMPRINT",EDGE,{"derivedFrom":subQ0}),1.0]])]})])],"isStart":true});var subQ6=sQuery(id+"F5.wireOp",EDGE,"E10");var subQ7=sQuery(id+"F5.wireOp",EDGE,"E11");var subQ8=sQuery(id+"F5.wireOp",EDGE,"E12");var subQ10=makeQuery(id+"F16.opPattern","COPY",FACE,{"derivedFrom":makeQuery(id+"F13.opLoft","SWEPT_FACE",FACE,{"disambiguationData":[OSD([subQ6,subQ7,subQ8,subQ1,subQ2,subQ3])]}),"instanceName":"13"});Q49=makeQuery(id+"F20.boolean.opBoolean","INTERSECT",EDGE,{"derivedFrom":[makeQuery(id+"F17.opBoolean","SPLIT",FACE,{"disambiguationData":[TD([makeQuery(id+"F16.opPattern","COPY",FACE,{"derivedFrom":subQ4,"instanceName":"13"})])],"derivedFrom":subQ10}),makeQuery(id+"F20.boolean.toolComplement.opBoolean","COPY",FACE,{"derivedFrom":makeQuery(id+"F20.opExtrude","SWEPT_FACE",FACE,{"disambiguationData":[OSD([sQuery(id+"F3.wireOp",EDGE,"E4")])]})})]});}
            var Q50;
            {var subQ0=sQuery(id+"F10.wireOp",EDGE,"E30");var subQ2=sQuery(id+"F10.wireOp",EDGE,"E32");var subQ3=sQuery(id+"F10.wireOp",EDGE,"E33");var subQ4=makeQuery(id+"F13.opLoft","CAP_FACE",FACE,{"disambiguationData":[OSD([makeQuery(id+"F10.imprint","IMPRINT",FACE,{"disambiguationData":[TD([[makeQuery(id+"F10.imprint","IMPRINT",EDGE,{"derivedFrom":subQ0}),1.0]])]})])],"isStart":true});var subQ5=sQuery(id+"F5.wireOp",EDGE,"E11");var subQ6=sQuery(id+"F5.wireOp",EDGE,"E10");var subQ7=sQuery(id+"F5.wireOp",EDGE,"E9");var subQ8=makeQuery(id+"F16.opPattern","COPY",FACE,{"derivedFrom":makeQuery(id+"F13.opLoft","SWEPT_FACE",FACE,{"disambiguationData":[OSD([subQ7,subQ6,subQ5,subQ0,subQ2,subQ3])]}),"instanceName":"13"});Q50=makeQuery(id+"F20.boolean.opBoolean","INTERSECT",EDGE,{"derivedFrom":[makeQuery(id+"F17.opBoolean","SPLIT",FACE,{"disambiguationData":[TD([makeQuery(id+"F16.opPattern","COPY",FACE,{"derivedFrom":subQ4,"instanceName":"13"})])],"derivedFrom":subQ8}),makeQuery(id+"F20.boolean.toolComplement.opBoolean","COPY",FACE,{"derivedFrom":makeQuery(id+"F20.opExtrude","SWEPT_FACE",FACE,{"disambiguationData":[OSD([sQuery(id+"F3.wireOp",EDGE,"E4")])]})})]});}
            var Q51;
            {var subQ0=sQuery(id+"F10.wireOp",EDGE,"E32");var subQ1=sQuery(id+"F10.wireOp",EDGE,"E31");var subQ2=sQuery(id+"F10.wireOp",EDGE,"E30");var subQ3=sQuery(id+"F5.wireOp",EDGE,"E12");var subQ4=sQuery(id+"F5.wireOp",EDGE,"E11");var subQ5=sQuery(id+"F5.wireOp",EDGE,"E9");var subQ6=makeQuery(id+"F16.opPattern","COPY",FACE,{"derivedFrom":makeQuery(id+"F13.opLoft","SWEPT_FACE",FACE,{"disambiguationData":[OSD([subQ5,subQ4,subQ3,subQ2,subQ1,subQ0])]}),"instanceName":"14"});var subQ8=makeQuery(id+"F13.opLoft","CAP_FACE",FACE,{"disambiguationData":[OSD([makeQuery(id+"F10.imprint","IMPRINT",FACE,{"disambiguationData":[TD([[makeQuery(id+"F10.imprint","IMPRINT",EDGE,{"derivedFrom":subQ2}),1.0]])]})])],"isStart":true});Q51=makeQuery(id+"F20.boolean.opBoolean","INTERSECT",EDGE,{"derivedFrom":[makeQuery(id+"F17.opBoolean","SPLIT",FACE,{"disambiguationData":[TD([makeQuery(id+"F16.opPattern","COPY",FACE,{"derivedFrom":subQ8,"instanceName":"13"})])],"derivedFrom":subQ6}),makeQuery(id+"F20.boolean.toolComplement.opBoolean","COPY",FACE,{"derivedFrom":makeQuery(id+"F20.opExtrude","SWEPT_FACE",FACE,{"disambiguationData":[OSD([sQuery(id+"F3.wireOp",EDGE,"E4")])]})})]});}
            var Q52;
            {var subQ0=sQuery(id+"F10.wireOp",EDGE,"E30");var subQ1=sQuery(id+"F10.wireOp",EDGE,"E31");var subQ3=sQuery(id+"F10.wireOp",EDGE,"E33");var subQ4=makeQuery(id+"F13.opLoft","CAP_FACE",FACE,{"disambiguationData":[OSD([makeQuery(id+"F10.imprint","IMPRINT",FACE,{"disambiguationData":[TD([[makeQuery(id+"F10.imprint","IMPRINT",EDGE,{"derivedFrom":subQ0}),1.0]])]})])],"isStart":true});var subQ6=sQuery(id+"F5.wireOp",EDGE,"E10");var subQ7=sQuery(id+"F5.wireOp",EDGE,"E9");var subQ9=sQuery(id+"F5.wireOp",EDGE,"E12");var subQ10=makeQuery(id+"F16.opPattern","COPY",FACE,{"derivedFrom":makeQuery(id+"F13.opLoft","SWEPT_FACE",FACE,{"disambiguationData":[OSD([subQ7,subQ6,subQ9,subQ0,subQ1,subQ3])]}),"instanceName":"14"});Q52=makeQuery(id+"F20.boolean.opBoolean","INTERSECT",EDGE,{"derivedFrom":[makeQuery(id+"F17.opBoolean","SPLIT",FACE,{"disambiguationData":[TD([makeQuery(id+"F16.opPattern","COPY",FACE,{"derivedFrom":subQ4,"instanceName":"13"})])],"derivedFrom":subQ10}),makeQuery(id+"F20.boolean.toolComplement.opBoolean","COPY",FACE,{"derivedFrom":makeQuery(id+"F20.opExtrude","SWEPT_FACE",FACE,{"disambiguationData":[OSD([sQuery(id+"F3.wireOp",EDGE,"E4")])]})})]});}
            var Q53;
            {var subQ1=sQuery(id+"F5.wireOp",EDGE,"E10");var subQ2=sQuery(id+"F5.wireOp",EDGE,"E11");var subQ3=sQuery(id+"F5.wireOp",EDGE,"E12");var subQ5=sQuery(id+"F10.wireOp",EDGE,"E32");var subQ6=sQuery(id+"F10.wireOp",EDGE,"E31");var subQ7=sQuery(id+"F10.wireOp",EDGE,"E30");var subQ9=sQuery(id+"F10.wireOp",EDGE,"E33");var subQ10=makeQuery(id+"F16.opPattern","COPY",FACE,{"derivedFrom":makeQuery(id+"F13.opLoft","SWEPT_FACE",FACE,{"disambiguationData":[OSD([subQ1,subQ2,subQ3,subQ6,subQ5,subQ9])]}),"instanceName":"14"});var subQ11=makeQuery(id+"F13.opLoft","CAP_FACE",FACE,{"disambiguationData":[OSD([makeQuery(id+"F10.imprint","IMPRINT",FACE,{"disambiguationData":[TD([[makeQuery(id+"F10.imprint","IMPRINT",EDGE,{"derivedFrom":subQ7}),1.0]])]})])],"isStart":true});Q53=makeQuery(id+"F20.boolean.opBoolean","INTERSECT",EDGE,{"derivedFrom":[makeQuery(id+"F17.opBoolean","SPLIT",FACE,{"disambiguationData":[TD([makeQuery(id+"F16.opPattern","COPY",FACE,{"derivedFrom":subQ11,"instanceName":"14"})])],"derivedFrom":subQ10}),makeQuery(id+"F20.boolean.toolComplement.opBoolean","COPY",FACE,{"derivedFrom":makeQuery(id+"F20.opExtrude","SWEPT_FACE",FACE,{"disambiguationData":[OSD([sQuery(id+"F3.wireOp",EDGE,"E4")])]})})]});}
            var Q54;
            {var subQ0=sQuery(id+"F10.wireOp",EDGE,"E30");var subQ2=sQuery(id+"F10.wireOp",EDGE,"E32");var subQ3=sQuery(id+"F10.wireOp",EDGE,"E33");var subQ4=makeQuery(id+"F13.opLoft","CAP_FACE",FACE,{"disambiguationData":[OSD([makeQuery(id+"F10.imprint","IMPRINT",FACE,{"disambiguationData":[TD([[makeQuery(id+"F10.imprint","IMPRINT",EDGE,{"derivedFrom":subQ0}),1.0]])]})])],"isStart":true});var subQ5=sQuery(id+"F5.wireOp",EDGE,"E11");var subQ6=sQuery(id+"F5.wireOp",EDGE,"E10");var subQ7=sQuery(id+"F5.wireOp",EDGE,"E9");var subQ8=makeQuery(id+"F16.opPattern","COPY",FACE,{"derivedFrom":makeQuery(id+"F13.opLoft","SWEPT_FACE",FACE,{"disambiguationData":[OSD([subQ7,subQ6,subQ5,subQ0,subQ2,subQ3])]}),"instanceName":"14"});Q54=makeQuery(id+"F20.boolean.opBoolean","INTERSECT",EDGE,{"derivedFrom":[makeQuery(id+"F17.opBoolean","SPLIT",FACE,{"disambiguationData":[TD([makeQuery(id+"F16.opPattern","COPY",FACE,{"derivedFrom":subQ4,"instanceName":"14"})])],"derivedFrom":subQ8}),makeQuery(id+"F20.boolean.toolComplement.opBoolean","COPY",FACE,{"derivedFrom":makeQuery(id+"F20.opExtrude","SWEPT_FACE",FACE,{"disambiguationData":[OSD([sQuery(id+"F3.wireOp",EDGE,"E4")])]})})]});}
            var Q55;
            {var subQ0=sQuery(id+"F10.wireOp",EDGE,"E32");var subQ1=sQuery(id+"F10.wireOp",EDGE,"E31");var subQ2=sQuery(id+"F10.wireOp",EDGE,"E30");var subQ3=sQuery(id+"F5.wireOp",EDGE,"E12");var subQ4=sQuery(id+"F5.wireOp",EDGE,"E11");var subQ5=sQuery(id+"F5.wireOp",EDGE,"E9");var subQ6=makeQuery(id+"F16.opPattern","COPY",FACE,{"derivedFrom":makeQuery(id+"F13.opLoft","SWEPT_FACE",FACE,{"disambiguationData":[OSD([subQ5,subQ4,subQ3,subQ2,subQ1,subQ0])]}),"instanceName":"15"});var subQ10=makeQuery(id+"F13.opLoft","CAP_FACE",FACE,{"disambiguationData":[OSD([makeQuery(id+"F10.imprint","IMPRINT",FACE,{"disambiguationData":[TD([[makeQuery(id+"F10.imprint","IMPRINT",EDGE,{"derivedFrom":subQ2}),1.0]])]})])],"isStart":true});Q55=makeQuery(id+"F20.boolean.opBoolean","INTERSECT",EDGE,{"derivedFrom":[makeQuery(id+"F17.opBoolean","SPLIT",FACE,{"disambiguationData":[TD([makeQuery(id+"F16.opPattern","COPY",FACE,{"derivedFrom":subQ10,"instanceName":"14"})])],"derivedFrom":subQ6}),makeQuery(id+"F20.boolean.toolComplement.opBoolean","COPY",FACE,{"derivedFrom":makeQuery(id+"F20.opExtrude","SWEPT_FACE",FACE,{"disambiguationData":[OSD([sQuery(id+"F3.wireOp",EDGE,"E4")])]})})]});}
            var Q56;
            {var subQ0=sQuery(id+"F10.wireOp",EDGE,"E33");var subQ1=sQuery(id+"F10.wireOp",EDGE,"E31");var subQ2=sQuery(id+"F10.wireOp",EDGE,"E30");var subQ3=sQuery(id+"F5.wireOp",EDGE,"E12");var subQ4=sQuery(id+"F5.wireOp",EDGE,"E10");var subQ5=sQuery(id+"F5.wireOp",EDGE,"E9");var subQ6=makeQuery(id+"F16.opPattern","COPY",FACE,{"derivedFrom":makeQuery(id+"F13.opLoft","SWEPT_FACE",FACE,{"disambiguationData":[OSD([subQ5,subQ4,subQ3,subQ2,subQ1,subQ0])]}),"instanceName":"15"});var subQ8=makeQuery(id+"F13.opLoft","CAP_FACE",FACE,{"disambiguationData":[OSD([makeQuery(id+"F10.imprint","IMPRINT",FACE,{"disambiguationData":[TD([[makeQuery(id+"F10.imprint","IMPRINT",EDGE,{"derivedFrom":subQ2}),1.0]])]})])],"isStart":true});Q56=makeQuery(id+"F20.boolean.opBoolean","INTERSECT",EDGE,{"derivedFrom":[makeQuery(id+"F17.opBoolean","SPLIT",FACE,{"disambiguationData":[TD([makeQuery(id+"F16.opPattern","COPY",FACE,{"derivedFrom":subQ8,"instanceName":"14"})])],"derivedFrom":subQ6}),makeQuery(id+"F20.boolean.toolComplement.opBoolean","COPY",FACE,{"derivedFrom":makeQuery(id+"F20.opExtrude","SWEPT_FACE",FACE,{"disambiguationData":[OSD([sQuery(id+"F3.wireOp",EDGE,"E4")])]})})]});}
            var Q57;
            {var subQ0=sQuery(id+"F10.wireOp",EDGE,"E30");var subQ1=sQuery(id+"F10.wireOp",EDGE,"E31");var subQ2=sQuery(id+"F10.wireOp",EDGE,"E32");var subQ3=sQuery(id+"F10.wireOp",EDGE,"E33");var subQ4=makeQuery(id+"F13.opLoft","CAP_FACE",FACE,{"disambiguationData":[OSD([makeQuery(id+"F10.imprint","IMPRINT",FACE,{"disambiguationData":[TD([[makeQuery(id+"F10.imprint","IMPRINT",EDGE,{"derivedFrom":subQ0}),1.0]])]})])],"isStart":true});var subQ6=sQuery(id+"F5.wireOp",EDGE,"E10");var subQ7=sQuery(id+"F5.wireOp",EDGE,"E11");var subQ8=sQuery(id+"F5.wireOp",EDGE,"E12");var subQ11=makeQuery(id+"F16.opPattern","COPY",FACE,{"derivedFrom":makeQuery(id+"F13.opLoft","SWEPT_FACE",FACE,{"disambiguationData":[OSD([subQ6,subQ7,subQ8,subQ1,subQ2,subQ3])]}),"instanceName":"15"});Q57=makeQuery(id+"F20.boolean.opBoolean","INTERSECT",EDGE,{"derivedFrom":[makeQuery(id+"F17.opBoolean","SPLIT",FACE,{"disambiguationData":[TD([makeQuery(id+"F16.opPattern","COPY",FACE,{"derivedFrom":subQ4,"instanceName":"15"})])],"derivedFrom":subQ11}),makeQuery(id+"F20.boolean.toolComplement.opBoolean","COPY",FACE,{"derivedFrom":makeQuery(id+"F20.opExtrude","SWEPT_FACE",FACE,{"disambiguationData":[OSD([sQuery(id+"F3.wireOp",EDGE,"E4")])]})})]});}
            var Q58;
            {var subQ0=sQuery(id+"F10.wireOp",EDGE,"E30");var subQ2=sQuery(id+"F10.wireOp",EDGE,"E32");var subQ3=sQuery(id+"F10.wireOp",EDGE,"E33");var subQ4=makeQuery(id+"F13.opLoft","CAP_FACE",FACE,{"disambiguationData":[OSD([makeQuery(id+"F10.imprint","IMPRINT",FACE,{"disambiguationData":[TD([[makeQuery(id+"F10.imprint","IMPRINT",EDGE,{"derivedFrom":subQ0}),1.0]])]})])],"isStart":true});var subQ5=sQuery(id+"F5.wireOp",EDGE,"E9");var subQ6=sQuery(id+"F5.wireOp",EDGE,"E10");var subQ7=sQuery(id+"F5.wireOp",EDGE,"E11");var subQ10=makeQuery(id+"F16.opPattern","COPY",FACE,{"derivedFrom":makeQuery(id+"F13.opLoft","SWEPT_FACE",FACE,{"disambiguationData":[OSD([subQ5,subQ6,subQ7,subQ0,subQ2,subQ3])]}),"instanceName":"15"});Q58=makeQuery(id+"F20.boolean.opBoolean","INTERSECT",EDGE,{"derivedFrom":[makeQuery(id+"F17.opBoolean","SPLIT",FACE,{"disambiguationData":[TD([makeQuery(id+"F16.opPattern","COPY",FACE,{"derivedFrom":subQ4,"instanceName":"15"})])],"derivedFrom":subQ10}),makeQuery(id+"F20.boolean.toolComplement.opBoolean","COPY",FACE,{"derivedFrom":makeQuery(id+"F20.opExtrude","SWEPT_FACE",FACE,{"disambiguationData":[OSD([sQuery(id+"F3.wireOp",EDGE,"E4")])]})})]});}
            var Q59;
            {var subQ0=sQuery(id+"F10.wireOp",EDGE,"E30");var subQ1=sQuery(id+"F10.wireOp",EDGE,"E31");var subQ2=sQuery(id+"F10.wireOp",EDGE,"E32");var subQ4=makeQuery(id+"F13.opLoft","CAP_FACE",FACE,{"disambiguationData":[OSD([makeQuery(id+"F10.imprint","IMPRINT",FACE,{"disambiguationData":[TD([[makeQuery(id+"F10.imprint","IMPRINT",EDGE,{"derivedFrom":subQ0}),1.0]])]})])],"isStart":true});var subQ5=sQuery(id+"F5.wireOp",EDGE,"E9");var subQ7=sQuery(id+"F5.wireOp",EDGE,"E11");var subQ8=sQuery(id+"F5.wireOp",EDGE,"E12");var subQ10=makeQuery(id+"F16.opPattern","COPY",FACE,{"derivedFrom":makeQuery(id+"F13.opLoft","SWEPT_FACE",FACE,{"disambiguationData":[OSD([subQ5,subQ7,subQ8,subQ0,subQ1,subQ2])]}),"instanceName":"16"});Q59=makeQuery(id+"F20.boolean.opBoolean","INTERSECT",EDGE,{"derivedFrom":[makeQuery(id+"F17.opBoolean","SPLIT",FACE,{"disambiguationData":[TD([makeQuery(id+"F16.opPattern","COPY",FACE,{"derivedFrom":subQ4,"instanceName":"15"})])],"derivedFrom":subQ10}),makeQuery(id+"F20.boolean.toolComplement.opBoolean","COPY",FACE,{"derivedFrom":makeQuery(id+"F20.opExtrude","SWEPT_FACE",FACE,{"disambiguationData":[OSD([sQuery(id+"F3.wireOp",EDGE,"E4")])]})})]});}
            var Q60;
            {var subQ0=sQuery(id+"F10.wireOp",EDGE,"E30");var subQ1=sQuery(id+"F10.wireOp",EDGE,"E31");var subQ3=sQuery(id+"F10.wireOp",EDGE,"E33");var subQ4=makeQuery(id+"F13.opLoft","CAP_FACE",FACE,{"disambiguationData":[OSD([makeQuery(id+"F10.imprint","IMPRINT",FACE,{"disambiguationData":[TD([[makeQuery(id+"F10.imprint","IMPRINT",EDGE,{"derivedFrom":subQ0}),1.0]])]})])],"isStart":true});var subQ5=sQuery(id+"F5.wireOp",EDGE,"E12");var subQ6=sQuery(id+"F5.wireOp",EDGE,"E10");var subQ7=sQuery(id+"F5.wireOp",EDGE,"E9");var subQ8=makeQuery(id+"F16.opPattern","COPY",FACE,{"derivedFrom":makeQuery(id+"F13.opLoft","SWEPT_FACE",FACE,{"disambiguationData":[OSD([subQ7,subQ6,subQ5,subQ0,subQ1,subQ3])]}),"instanceName":"16"});Q60=makeQuery(id+"F20.boolean.opBoolean","INTERSECT",EDGE,{"derivedFrom":[makeQuery(id+"F17.opBoolean","SPLIT",FACE,{"disambiguationData":[TD([makeQuery(id+"F16.opPattern","COPY",FACE,{"derivedFrom":subQ4,"instanceName":"15"})])],"derivedFrom":subQ8}),makeQuery(id+"F20.boolean.toolComplement.opBoolean","COPY",FACE,{"derivedFrom":makeQuery(id+"F20.opExtrude","SWEPT_FACE",FACE,{"disambiguationData":[OSD([sQuery(id+"F3.wireOp",EDGE,"E4")])]})})]});}
            var Q61;
            {var subQ1=sQuery(id+"F5.wireOp",EDGE,"E10");var subQ2=sQuery(id+"F5.wireOp",EDGE,"E11");var subQ3=sQuery(id+"F5.wireOp",EDGE,"E12");var subQ5=sQuery(id+"F10.wireOp",EDGE,"E30");var subQ6=sQuery(id+"F10.wireOp",EDGE,"E31");var subQ7=sQuery(id+"F10.wireOp",EDGE,"E32");var subQ8=sQuery(id+"F10.wireOp",EDGE,"E33");var subQ9=makeQuery(id+"F13.opLoft","CAP_FACE",FACE,{"disambiguationData":[OSD([makeQuery(id+"F10.imprint","IMPRINT",FACE,{"disambiguationData":[TD([[makeQuery(id+"F10.imprint","IMPRINT",EDGE,{"derivedFrom":subQ5}),1.0]])]})])],"isStart":true});var subQ10=makeQuery(id+"F16.opPattern","COPY",FACE,{"derivedFrom":makeQuery(id+"F13.opLoft","SWEPT_FACE",FACE,{"disambiguationData":[OSD([subQ1,subQ2,subQ3,subQ6,subQ7,subQ8])]}),"instanceName":"16"});Q61=makeQuery(id+"F20.boolean.opBoolean","INTERSECT",EDGE,{"derivedFrom":[makeQuery(id+"F17.opBoolean","SPLIT",FACE,{"disambiguationData":[TD([makeQuery(id+"F16.opPattern","COPY",FACE,{"derivedFrom":subQ9,"instanceName":"16"})])],"derivedFrom":subQ10}),makeQuery(id+"F20.boolean.toolComplement.opBoolean","COPY",FACE,{"derivedFrom":makeQuery(id+"F20.opExtrude","SWEPT_FACE",FACE,{"disambiguationData":[OSD([sQuery(id+"F3.wireOp",EDGE,"E4")])]})})]});}
            var Q62;
            {var subQ0=sQuery(id+"F10.wireOp",EDGE,"E30");var subQ2=sQuery(id+"F10.wireOp",EDGE,"E32");var subQ3=sQuery(id+"F10.wireOp",EDGE,"E33");var subQ4=makeQuery(id+"F13.opLoft","CAP_FACE",FACE,{"disambiguationData":[OSD([makeQuery(id+"F10.imprint","IMPRINT",FACE,{"disambiguationData":[TD([[makeQuery(id+"F10.imprint","IMPRINT",EDGE,{"derivedFrom":subQ0}),1.0]])]})])],"isStart":true});var subQ5=sQuery(id+"F5.wireOp",EDGE,"E9");var subQ6=sQuery(id+"F5.wireOp",EDGE,"E10");var subQ7=sQuery(id+"F5.wireOp",EDGE,"E11");var subQ10=makeQuery(id+"F16.opPattern","COPY",FACE,{"derivedFrom":makeQuery(id+"F13.opLoft","SWEPT_FACE",FACE,{"disambiguationData":[OSD([subQ5,subQ6,subQ7,subQ0,subQ2,subQ3])]}),"instanceName":"16"});Q62=makeQuery(id+"F20.boolean.opBoolean","INTERSECT",EDGE,{"derivedFrom":[makeQuery(id+"F17.opBoolean","SPLIT",FACE,{"disambiguationData":[TD([makeQuery(id+"F16.opPattern","COPY",FACE,{"derivedFrom":subQ4,"instanceName":"16"})])],"derivedFrom":subQ10}),makeQuery(id+"F20.boolean.toolComplement.opBoolean","COPY",FACE,{"derivedFrom":makeQuery(id+"F20.opExtrude","SWEPT_FACE",FACE,{"disambiguationData":[OSD([sQuery(id+"F3.wireOp",EDGE,"E4")])]})})]});}
            var Q63;
            {var subQ0=sQuery(id+"F10.wireOp",EDGE,"E32");var subQ1=sQuery(id+"F10.wireOp",EDGE,"E31");var subQ2=sQuery(id+"F10.wireOp",EDGE,"E30");var subQ3=sQuery(id+"F5.wireOp",EDGE,"E12");var subQ4=sQuery(id+"F5.wireOp",EDGE,"E11");var subQ5=sQuery(id+"F5.wireOp",EDGE,"E9");var subQ6=makeQuery(id+"F16.opPattern","COPY",FACE,{"derivedFrom":makeQuery(id+"F13.opLoft","SWEPT_FACE",FACE,{"disambiguationData":[OSD([subQ5,subQ4,subQ3,subQ2,subQ1,subQ0])]}),"instanceName":"17"});var subQ10=makeQuery(id+"F13.opLoft","CAP_FACE",FACE,{"disambiguationData":[OSD([makeQuery(id+"F10.imprint","IMPRINT",FACE,{"disambiguationData":[TD([[makeQuery(id+"F10.imprint","IMPRINT",EDGE,{"derivedFrom":subQ2}),1.0]])]})])],"isStart":true});Q63=makeQuery(id+"F20.boolean.opBoolean","INTERSECT",EDGE,{"derivedFrom":[makeQuery(id+"F17.opBoolean","SPLIT",FACE,{"disambiguationData":[TD([makeQuery(id+"F16.opPattern","COPY",FACE,{"derivedFrom":subQ10,"instanceName":"16"})])],"derivedFrom":subQ6}),makeQuery(id+"F20.boolean.toolComplement.opBoolean","COPY",FACE,{"derivedFrom":makeQuery(id+"F20.opExtrude","SWEPT_FACE",FACE,{"disambiguationData":[OSD([sQuery(id+"F3.wireOp",EDGE,"E4")])]})})]});}
            var Q64;
            {var subQ0=sQuery(id+"F10.wireOp",EDGE,"E33");var subQ1=sQuery(id+"F10.wireOp",EDGE,"E31");var subQ2=sQuery(id+"F10.wireOp",EDGE,"E30");var subQ3=sQuery(id+"F5.wireOp",EDGE,"E12");var subQ4=sQuery(id+"F5.wireOp",EDGE,"E10");var subQ5=sQuery(id+"F5.wireOp",EDGE,"E9");var subQ6=makeQuery(id+"F16.opPattern","COPY",FACE,{"derivedFrom":makeQuery(id+"F13.opLoft","SWEPT_FACE",FACE,{"disambiguationData":[OSD([subQ5,subQ4,subQ3,subQ2,subQ1,subQ0])]}),"instanceName":"17"});var subQ8=makeQuery(id+"F13.opLoft","CAP_FACE",FACE,{"disambiguationData":[OSD([makeQuery(id+"F10.imprint","IMPRINT",FACE,{"disambiguationData":[TD([[makeQuery(id+"F10.imprint","IMPRINT",EDGE,{"derivedFrom":subQ2}),1.0]])]})])],"isStart":true});Q64=makeQuery(id+"F20.boolean.opBoolean","INTERSECT",EDGE,{"derivedFrom":[makeQuery(id+"F17.opBoolean","SPLIT",FACE,{"disambiguationData":[TD([makeQuery(id+"F16.opPattern","COPY",FACE,{"derivedFrom":subQ8,"instanceName":"16"})])],"derivedFrom":subQ6}),makeQuery(id+"F20.boolean.toolComplement.opBoolean","COPY",FACE,{"derivedFrom":makeQuery(id+"F20.opExtrude","SWEPT_FACE",FACE,{"disambiguationData":[OSD([sQuery(id+"F3.wireOp",EDGE,"E4")])]})})]});}
            var Q65;
            {var subQ1=sQuery(id+"F5.wireOp",EDGE,"E10");var subQ2=sQuery(id+"F5.wireOp",EDGE,"E11");var subQ3=sQuery(id+"F5.wireOp",EDGE,"E12");var subQ5=sQuery(id+"F10.wireOp",EDGE,"E33");var subQ6=sQuery(id+"F10.wireOp",EDGE,"E32");var subQ7=sQuery(id+"F10.wireOp",EDGE,"E31");var subQ8=makeQuery(id+"F16.opPattern","COPY",FACE,{"derivedFrom":makeQuery(id+"F13.opLoft","SWEPT_FACE",FACE,{"disambiguationData":[OSD([subQ1,subQ2,subQ3,subQ7,subQ6,subQ5])]}),"instanceName":"17"});var subQ9=sQuery(id+"F10.wireOp",EDGE,"E30");var subQ11=makeQuery(id+"F13.opLoft","CAP_FACE",FACE,{"disambiguationData":[OSD([makeQuery(id+"F10.imprint","IMPRINT",FACE,{"disambiguationData":[TD([[makeQuery(id+"F10.imprint","IMPRINT",EDGE,{"derivedFrom":subQ9}),1.0]])]})])],"isStart":true});Q65=makeQuery(id+"F20.boolean.opBoolean","INTERSECT",EDGE,{"derivedFrom":[makeQuery(id+"F17.opBoolean","SPLIT",FACE,{"disambiguationData":[TD([subQ11])],"derivedFrom":subQ8}),makeQuery(id+"F20.boolean.toolComplement.opBoolean","COPY",FACE,{"derivedFrom":makeQuery(id+"F20.opExtrude","SWEPT_FACE",FACE,{"disambiguationData":[OSD([sQuery(id+"F3.wireOp",EDGE,"E4")])]})})]});}
            var Q66;
            {var subQ0=sQuery(id+"F10.wireOp",EDGE,"E33");var subQ2=sQuery(id+"F10.wireOp",EDGE,"E30");var subQ4=sQuery(id+"F5.wireOp",EDGE,"E10");var subQ5=sQuery(id+"F5.wireOp",EDGE,"E9");var subQ7=sQuery(id+"F5.wireOp",EDGE,"E11");var subQ9=sQuery(id+"F10.wireOp",EDGE,"E32");var subQ10=makeQuery(id+"F13.opLoft","CAP_FACE",FACE,{"disambiguationData":[OSD([makeQuery(id+"F10.imprint","IMPRINT",FACE,{"disambiguationData":[TD([[makeQuery(id+"F10.imprint","IMPRINT",EDGE,{"derivedFrom":subQ2}),1.0]])]})])],"isStart":true});var subQ11=makeQuery(id+"F16.opPattern","COPY",FACE,{"derivedFrom":makeQuery(id+"F13.opLoft","SWEPT_FACE",FACE,{"disambiguationData":[OSD([subQ5,subQ4,subQ7,subQ2,subQ9,subQ0])]}),"instanceName":"17"});Q66=makeQuery(id+"F20.boolean.opBoolean","INTERSECT",EDGE,{"derivedFrom":[makeQuery(id+"F17.opBoolean","SPLIT",FACE,{"disambiguationData":[TD([subQ10])],"derivedFrom":subQ11}),makeQuery(id+"F20.boolean.toolComplement.opBoolean","COPY",FACE,{"derivedFrom":makeQuery(id+"F20.opExtrude","SWEPT_FACE",FACE,{"disambiguationData":[OSD([sQuery(id+"F3.wireOp",EDGE,"E4")])]})})]});}
            var Q67;
            {var subQ0=sQuery(id+"F5.wireOp",EDGE,"E9");var subQ2=sQuery(id+"F5.wireOp",EDGE,"E11");var subQ3=sQuery(id+"F5.wireOp",EDGE,"E12");var subQ6=sQuery(id+"F10.wireOp",EDGE,"E32");var subQ7=sQuery(id+"F10.wireOp",EDGE,"E31");var subQ9=sQuery(id+"F10.wireOp",EDGE,"E30");var subQ10=makeQuery(id+"F13.opLoft","CAP_FACE",FACE,{"disambiguationData":[OSD([makeQuery(id+"F10.imprint","IMPRINT",FACE,{"disambiguationData":[TD([[makeQuery(id+"F10.imprint","IMPRINT",EDGE,{"derivedFrom":subQ9}),1.0]])]})])],"isStart":true});var subQ11=makeQuery(id+"F13.opLoft","SWEPT_FACE",FACE,{"disambiguationData":[OSD([subQ0,subQ2,subQ3,subQ9,subQ7,subQ6])]});Q67=makeQuery(id+"F20.boolean.opBoolean","INTERSECT",EDGE,{"derivedFrom":[makeQuery(id+"F17.opBoolean","SPLIT",FACE,{"disambiguationData":[TD([subQ10])],"derivedFrom":subQ11}),makeQuery(id+"F20.boolean.toolComplement.opBoolean","COPY",FACE,{"derivedFrom":makeQuery(id+"F20.opExtrude","SWEPT_FACE",FACE,{"disambiguationData":[OSD([sQuery(id+"F3.wireOp",EDGE,"E4")])]})})]});}
            var Q68;
            {var subQ0=sQuery(id+"F10.wireOp",EDGE,"E30");var subQ2=sQuery(id+"F10.wireOp",EDGE,"E32");var subQ3=sQuery(id+"F10.wireOp",EDGE,"E33");var subQ4=makeQuery(id+"F13.opLoft","CAP_FACE",FACE,{"disambiguationData":[OSD([makeQuery(id+"F10.imprint","IMPRINT",FACE,{"disambiguationData":[TD([[makeQuery(id+"F10.imprint","IMPRINT",EDGE,{"derivedFrom":subQ0}),1.0]])]})])],"isStart":true});var subQ6=sQuery(id+"F5.wireOp",EDGE,"E10");var subQ7=sQuery(id+"F5.wireOp",EDGE,"E9");var subQ9=sQuery(id+"F5.wireOp",EDGE,"E11");var subQ11=makeQuery(id+"F13.opLoft","SWEPT_FACE",FACE,{"disambiguationData":[OSD([subQ7,subQ6,subQ9,subQ0,subQ2,subQ3])]});Q68=makeQuery(id+"F20.boolean.opBoolean","INTERSECT",EDGE,{"derivedFrom":[makeQuery(id+"F17.opBoolean","SPLIT",FACE,{"disambiguationData":[TD([subQ4])],"derivedFrom":subQ11}),makeQuery(id+"F20.boolean.toolComplement.opBoolean","COPY",FACE,{"derivedFrom":makeQuery(id+"F20.opExtrude","SWEPT_FACE",FACE,{"disambiguationData":[OSD([sQuery(id+"F3.wireOp",EDGE,"E4")])]})})]});}
            var Q69;
            {var subQ0=sQuery(id+"F10.wireOp",EDGE,"E30");var subQ1=sQuery(id+"F10.wireOp",EDGE,"E31");var subQ3=sQuery(id+"F10.wireOp",EDGE,"E33");var subQ4=makeQuery(id+"F13.opLoft","CAP_FACE",FACE,{"disambiguationData":[OSD([makeQuery(id+"F10.imprint","IMPRINT",FACE,{"disambiguationData":[TD([[makeQuery(id+"F10.imprint","IMPRINT",EDGE,{"derivedFrom":subQ0}),1.0]])]})])],"isStart":true});var subQ5=sQuery(id+"F5.wireOp",EDGE,"E12");var subQ6=sQuery(id+"F5.wireOp",EDGE,"E10");var subQ7=sQuery(id+"F5.wireOp",EDGE,"E9");var subQ8=makeQuery(id+"F13.opLoft","SWEPT_FACE",FACE,{"disambiguationData":[OSD([subQ7,subQ6,subQ5,subQ0,subQ1,subQ3])]});Q69=makeQuery(id+"F20.boolean.opBoolean","INTERSECT",EDGE,{"derivedFrom":[makeQuery(id+"F17.opBoolean","SPLIT",FACE,{"disambiguationData":[TD([subQ4])],"derivedFrom":subQ8}),makeQuery(id+"F20.boolean.toolComplement.opBoolean","COPY",FACE,{"derivedFrom":makeQuery(id+"F20.opExtrude","SWEPT_FACE",FACE,{"disambiguationData":[OSD([sQuery(id+"F3.wireOp",EDGE,"E4")])]})})]});}
            var Q70;
            {var subQ1=sQuery(id+"F5.wireOp",EDGE,"E10");var subQ2=sQuery(id+"F5.wireOp",EDGE,"E11");var subQ3=sQuery(id+"F5.wireOp",EDGE,"E12");var subQ5=sQuery(id+"F10.wireOp",EDGE,"E30");var subQ6=sQuery(id+"F10.wireOp",EDGE,"E31");var subQ7=sQuery(id+"F10.wireOp",EDGE,"E32");var subQ8=sQuery(id+"F10.wireOp",EDGE,"E33");var subQ9=makeQuery(id+"F13.opLoft","CAP_FACE",FACE,{"disambiguationData":[OSD([makeQuery(id+"F10.imprint","IMPRINT",FACE,{"disambiguationData":[TD([[makeQuery(id+"F10.imprint","IMPRINT",EDGE,{"derivedFrom":subQ5}),1.0]])]})])],"isStart":true});var subQ10=makeQuery(id+"F13.opLoft","SWEPT_FACE",FACE,{"disambiguationData":[OSD([subQ1,subQ2,subQ3,subQ6,subQ7,subQ8])]});Q70=makeQuery(id+"F20.boolean.opBoolean","INTERSECT",EDGE,{"derivedFrom":[makeQuery(id+"F17.opBoolean","SPLIT",FACE,{"disambiguationData":[TD([subQ9])],"derivedFrom":subQ10}),makeQuery(id+"F20.boolean.toolComplement.opBoolean","COPY",FACE,{"derivedFrom":makeQuery(id+"F20.opExtrude","SWEPT_FACE",FACE,{"disambiguationData":[OSD([sQuery(id+"F3.wireOp",EDGE,"E4")])]})})]});}
            var Q71;
            {var subQ0=sQuery(id+"F10.wireOp",EDGE,"E32");var subQ1=sQuery(id+"F10.wireOp",EDGE,"E31");var subQ2=sQuery(id+"F10.wireOp",EDGE,"E30");var subQ3=sQuery(id+"F5.wireOp",EDGE,"E12");var subQ4=sQuery(id+"F5.wireOp",EDGE,"E11");var subQ5=sQuery(id+"F5.wireOp",EDGE,"E9");var subQ6=makeQuery(id+"F16.opPattern","COPY",FACE,{"derivedFrom":makeQuery(id+"F13.opLoft","SWEPT_FACE",FACE,{"disambiguationData":[OSD([subQ5,subQ4,subQ3,subQ2,subQ1,subQ0])]}),"instanceName":"1"});var subQ11=makeQuery(id+"F13.opLoft","CAP_FACE",FACE,{"disambiguationData":[OSD([makeQuery(id+"F10.imprint","IMPRINT",FACE,{"disambiguationData":[TD([[makeQuery(id+"F10.imprint","IMPRINT",EDGE,{"derivedFrom":subQ2}),1.0]])]})])],"isStart":true});Q71=makeQuery(id+"F20.boolean.opBoolean","INTERSECT",EDGE,{"derivedFrom":[makeQuery(id+"F17.opBoolean","SPLIT",FACE,{"disambiguationData":[TD([subQ11])],"derivedFrom":subQ6}),makeQuery(id+"F20.boolean.toolComplement.opBoolean","COPY",FACE,{"derivedFrom":makeQuery(id+"F20.opExtrude","SWEPT_FACE",FACE,{"disambiguationData":[OSD([sQuery(id+"F3.wireOp",EDGE,"E4")])]})})]});}
            var Q72;
            {var subQ0=sQuery(id+"F10.wireOp",EDGE,"E33");var subQ1=sQuery(id+"F10.wireOp",EDGE,"E31");var subQ2=sQuery(id+"F10.wireOp",EDGE,"E30");var subQ3=sQuery(id+"F5.wireOp",EDGE,"E12");var subQ4=sQuery(id+"F5.wireOp",EDGE,"E10");var subQ5=sQuery(id+"F5.wireOp",EDGE,"E9");var subQ6=makeQuery(id+"F16.opPattern","COPY",FACE,{"derivedFrom":makeQuery(id+"F13.opLoft","SWEPT_FACE",FACE,{"disambiguationData":[OSD([subQ5,subQ4,subQ3,subQ2,subQ1,subQ0])]}),"instanceName":"1"});var subQ10=makeQuery(id+"F13.opLoft","CAP_FACE",FACE,{"disambiguationData":[OSD([makeQuery(id+"F10.imprint","IMPRINT",FACE,{"disambiguationData":[TD([[makeQuery(id+"F10.imprint","IMPRINT",EDGE,{"derivedFrom":subQ2}),1.0]])]})])],"isStart":true});Q72=makeQuery(id+"F20.boolean.opBoolean","INTERSECT",EDGE,{"derivedFrom":[makeQuery(id+"F17.opBoolean","SPLIT",FACE,{"disambiguationData":[TD([subQ10])],"derivedFrom":subQ6}),makeQuery(id+"F20.boolean.toolComplement.opBoolean","COPY",FACE,{"derivedFrom":makeQuery(id+"F20.opExtrude","SWEPT_FACE",FACE,{"disambiguationData":[OSD([sQuery(id+"F3.wireOp",EDGE,"E4")])]})})]});}
            var Q73;
            {var subQ1=sQuery(id+"F5.wireOp",EDGE,"E10");var subQ2=sQuery(id+"F5.wireOp",EDGE,"E11");var subQ3=sQuery(id+"F5.wireOp",EDGE,"E12");var subQ5=sQuery(id+"F10.wireOp",EDGE,"E30");var subQ6=sQuery(id+"F10.wireOp",EDGE,"E31");var subQ7=sQuery(id+"F10.wireOp",EDGE,"E32");var subQ8=sQuery(id+"F10.wireOp",EDGE,"E33");var subQ9=makeQuery(id+"F13.opLoft","CAP_FACE",FACE,{"disambiguationData":[OSD([makeQuery(id+"F10.imprint","IMPRINT",FACE,{"disambiguationData":[TD([[makeQuery(id+"F10.imprint","IMPRINT",EDGE,{"derivedFrom":subQ5}),1.0]])]})])],"isStart":true});var subQ10=makeQuery(id+"F16.opPattern","COPY",FACE,{"derivedFrom":makeQuery(id+"F13.opLoft","SWEPT_FACE",FACE,{"disambiguationData":[OSD([subQ1,subQ2,subQ3,subQ6,subQ7,subQ8])]}),"instanceName":"1"});Q73=makeQuery(id+"F20.boolean.opBoolean","INTERSECT",EDGE,{"derivedFrom":[makeQuery(id+"F17.opBoolean","SPLIT",FACE,{"disambiguationData":[TD([makeQuery(id+"F16.opPattern","COPY",FACE,{"derivedFrom":subQ9,"instanceName":"1"})])],"derivedFrom":subQ10}),makeQuery(id+"F20.boolean.toolComplement.opBoolean","COPY",FACE,{"derivedFrom":makeQuery(id+"F20.opExtrude","SWEPT_FACE",FACE,{"disambiguationData":[OSD([sQuery(id+"F3.wireOp",EDGE,"E4")])]})})]});}
            var Q74;
            {var subQ0=sQuery(id+"F10.wireOp",EDGE,"E30");var subQ2=sQuery(id+"F10.wireOp",EDGE,"E32");var subQ3=sQuery(id+"F10.wireOp",EDGE,"E33");var subQ4=makeQuery(id+"F13.opLoft","CAP_FACE",FACE,{"disambiguationData":[OSD([makeQuery(id+"F10.imprint","IMPRINT",FACE,{"disambiguationData":[TD([[makeQuery(id+"F10.imprint","IMPRINT",EDGE,{"derivedFrom":subQ0}),1.0]])]})])],"isStart":true});var subQ6=sQuery(id+"F5.wireOp",EDGE,"E10");var subQ7=sQuery(id+"F5.wireOp",EDGE,"E9");var subQ9=sQuery(id+"F5.wireOp",EDGE,"E11");var subQ11=makeQuery(id+"F16.opPattern","COPY",FACE,{"derivedFrom":makeQuery(id+"F13.opLoft","SWEPT_FACE",FACE,{"disambiguationData":[OSD([subQ7,subQ6,subQ9,subQ0,subQ2,subQ3])]}),"instanceName":"1"});Q74=makeQuery(id+"F20.boolean.opBoolean","INTERSECT",EDGE,{"derivedFrom":[makeQuery(id+"F17.opBoolean","SPLIT",FACE,{"disambiguationData":[TD([makeQuery(id+"F16.opPattern","COPY",FACE,{"derivedFrom":subQ4,"instanceName":"1"})])],"derivedFrom":subQ11}),makeQuery(id+"F20.boolean.toolComplement.opBoolean","COPY",FACE,{"derivedFrom":makeQuery(id+"F20.opExtrude","SWEPT_FACE",FACE,{"disambiguationData":[OSD([sQuery(id+"F3.wireOp",EDGE,"E4")])]})})]});}
            var Q75;
            {var subQ0=sQuery(id+"F5.wireOp",EDGE,"E9");var subQ2=sQuery(id+"F5.wireOp",EDGE,"E11");var subQ3=sQuery(id+"F5.wireOp",EDGE,"E12");var subQ5=sQuery(id+"F10.wireOp",EDGE,"E32");var subQ6=sQuery(id+"F10.wireOp",EDGE,"E31");var subQ7=sQuery(id+"F10.wireOp",EDGE,"E30");var subQ8=makeQuery(id+"F16.opPattern","COPY",FACE,{"derivedFrom":makeQuery(id+"F13.opLoft","SWEPT_FACE",FACE,{"disambiguationData":[OSD([subQ0,subQ2,subQ3,subQ7,subQ6,subQ5])]}),"instanceName":"2"});var subQ10=makeQuery(id+"F13.opLoft","CAP_FACE",FACE,{"disambiguationData":[OSD([makeQuery(id+"F10.imprint","IMPRINT",FACE,{"disambiguationData":[TD([[makeQuery(id+"F10.imprint","IMPRINT",EDGE,{"derivedFrom":subQ7}),1.0]])]})])],"isStart":true});Q75=makeQuery(id+"F20.boolean.opBoolean","INTERSECT",EDGE,{"derivedFrom":[makeQuery(id+"F17.opBoolean","SPLIT",FACE,{"disambiguationData":[TD([makeQuery(id+"F16.opPattern","COPY",FACE,{"derivedFrom":subQ10,"instanceName":"1"})])],"derivedFrom":subQ8}),makeQuery(id+"F20.boolean.toolComplement.opBoolean","COPY",FACE,{"derivedFrom":makeQuery(id+"F20.opExtrude","SWEPT_FACE",FACE,{"disambiguationData":[OSD([sQuery(id+"F3.wireOp",EDGE,"E4")])]})})]});}
            var Q76;
            {var subQ0=sQuery(id+"F10.wireOp",EDGE,"E30");var subQ1=sQuery(id+"F10.wireOp",EDGE,"E31");var subQ3=sQuery(id+"F10.wireOp",EDGE,"E33");var subQ4=makeQuery(id+"F13.opLoft","CAP_FACE",FACE,{"disambiguationData":[OSD([makeQuery(id+"F10.imprint","IMPRINT",FACE,{"disambiguationData":[TD([[makeQuery(id+"F10.imprint","IMPRINT",EDGE,{"derivedFrom":subQ0}),1.0]])]})])],"isStart":true});var subQ5=sQuery(id+"F5.wireOp",EDGE,"E12");var subQ6=sQuery(id+"F5.wireOp",EDGE,"E10");var subQ7=sQuery(id+"F5.wireOp",EDGE,"E9");var subQ8=makeQuery(id+"F16.opPattern","COPY",FACE,{"derivedFrom":makeQuery(id+"F13.opLoft","SWEPT_FACE",FACE,{"disambiguationData":[OSD([subQ7,subQ6,subQ5,subQ0,subQ1,subQ3])]}),"instanceName":"2"});Q76=makeQuery(id+"F20.boolean.opBoolean","INTERSECT",EDGE,{"derivedFrom":[makeQuery(id+"F17.opBoolean","SPLIT",FACE,{"disambiguationData":[TD([makeQuery(id+"F16.opPattern","COPY",FACE,{"derivedFrom":subQ4,"instanceName":"1"})])],"derivedFrom":subQ8}),makeQuery(id+"F20.boolean.toolComplement.opBoolean","COPY",FACE,{"derivedFrom":makeQuery(id+"F20.opExtrude","SWEPT_FACE",FACE,{"disambiguationData":[OSD([sQuery(id+"F3.wireOp",EDGE,"E4")])]})})]});}
            var Q77;
            {var subQ1=sQuery(id+"F5.wireOp",EDGE,"E10");var subQ2=sQuery(id+"F5.wireOp",EDGE,"E11");var subQ3=sQuery(id+"F5.wireOp",EDGE,"E12");var subQ5=sQuery(id+"F10.wireOp",EDGE,"E30");var subQ6=sQuery(id+"F10.wireOp",EDGE,"E31");var subQ7=sQuery(id+"F10.wireOp",EDGE,"E32");var subQ8=sQuery(id+"F10.wireOp",EDGE,"E33");var subQ9=makeQuery(id+"F13.opLoft","CAP_FACE",FACE,{"disambiguationData":[OSD([makeQuery(id+"F10.imprint","IMPRINT",FACE,{"disambiguationData":[TD([[makeQuery(id+"F10.imprint","IMPRINT",EDGE,{"derivedFrom":subQ5}),1.0]])]})])],"isStart":true});var subQ10=makeQuery(id+"F16.opPattern","COPY",FACE,{"derivedFrom":makeQuery(id+"F13.opLoft","SWEPT_FACE",FACE,{"disambiguationData":[OSD([subQ1,subQ2,subQ3,subQ6,subQ7,subQ8])]}),"instanceName":"2"});Q77=makeQuery(id+"F20.boolean.opBoolean","INTERSECT",EDGE,{"derivedFrom":[makeQuery(id+"F17.opBoolean","SPLIT",FACE,{"disambiguationData":[TD([makeQuery(id+"F16.opPattern","COPY",FACE,{"derivedFrom":subQ9,"instanceName":"2"})])],"derivedFrom":subQ10}),makeQuery(id+"F20.boolean.toolComplement.opBoolean","COPY",FACE,{"derivedFrom":makeQuery(id+"F20.opExtrude","SWEPT_FACE",FACE,{"disambiguationData":[OSD([sQuery(id+"F3.wireOp",EDGE,"E4")])]})})]});}
            var Q78;
            {var subQ0=sQuery(id+"F10.wireOp",EDGE,"E30");var subQ2=sQuery(id+"F10.wireOp",EDGE,"E32");var subQ3=sQuery(id+"F10.wireOp",EDGE,"E33");var subQ4=makeQuery(id+"F13.opLoft","CAP_FACE",FACE,{"disambiguationData":[OSD([makeQuery(id+"F10.imprint","IMPRINT",FACE,{"disambiguationData":[TD([[makeQuery(id+"F10.imprint","IMPRINT",EDGE,{"derivedFrom":subQ0}),1.0]])]})])],"isStart":true});var subQ5=sQuery(id+"F5.wireOp",EDGE,"E9");var subQ6=sQuery(id+"F5.wireOp",EDGE,"E10");var subQ7=sQuery(id+"F5.wireOp",EDGE,"E11");var subQ10=makeQuery(id+"F16.opPattern","COPY",FACE,{"derivedFrom":makeQuery(id+"F13.opLoft","SWEPT_FACE",FACE,{"disambiguationData":[OSD([subQ5,subQ6,subQ7,subQ0,subQ2,subQ3])]}),"instanceName":"2"});Q78=makeQuery(id+"F20.boolean.opBoolean","INTERSECT",EDGE,{"derivedFrom":[makeQuery(id+"F17.opBoolean","SPLIT",FACE,{"disambiguationData":[TD([makeQuery(id+"F16.opPattern","COPY",FACE,{"derivedFrom":subQ4,"instanceName":"2"})])],"derivedFrom":subQ10}),makeQuery(id+"F20.boolean.toolComplement.opBoolean","COPY",FACE,{"derivedFrom":makeQuery(id+"F20.opExtrude","SWEPT_FACE",FACE,{"disambiguationData":[OSD([sQuery(id+"F3.wireOp",EDGE,"E4")])]})})]});}
            var Q79;
            Q79=makeQuery(id+"F16.opPattern","COPY",EDGE,{"derivedFrom":makeQuery(id+"F13.opLoft","SWEPT_EDGE",EDGE,{"disambiguationData":[OSD([sQuery(id+"F5.wireOp",EDGE,"E11"),sQuery(id+"F5.wireOp",EDGE,"E12"),sQuery(id+"F10.wireOp",EDGE,"E31"),sQuery(id+"F10.wireOp",EDGE,"E32")])]}),"instanceName":"2"});
            var Q80;
            Q80=makeQuery(id+"F16.opPattern","COPY",EDGE,{"derivedFrom":makeQuery(id+"F13.opLoft","SWEPT_EDGE",EDGE,{"disambiguationData":[OSD([sQuery(id+"F5.wireOp",EDGE,"E11"),sQuery(id+"F5.wireOp",EDGE,"E12"),sQuery(id+"F10.wireOp",EDGE,"E31"),sQuery(id+"F10.wireOp",EDGE,"E32")])]}),"instanceName":"1"});
            var Q81;
            Q81=makeQuery(id+"F13.opLoft","SWEPT_EDGE",EDGE,{"disambiguationData":[OSD([sQuery(id+"F5.wireOp",EDGE,"E11"),sQuery(id+"F5.wireOp",EDGE,"E12"),sQuery(id+"F10.wireOp",EDGE,"E31"),sQuery(id+"F10.wireOp",EDGE,"E32")])]});
            var Q82;
            Q82=makeQuery(id+"F16.opPattern","COPY",EDGE,{"derivedFrom":makeQuery(id+"F13.opLoft","SWEPT_EDGE",EDGE,{"disambiguationData":[OSD([sQuery(id+"F5.wireOp",EDGE,"E11"),sQuery(id+"F5.wireOp",EDGE,"E12"),sQuery(id+"F10.wireOp",EDGE,"E31"),sQuery(id+"F10.wireOp",EDGE,"E32")])]}),"instanceName":"17"});
            var Q83;
            Q83=makeQuery(id+"F16.opPattern","COPY",EDGE,{"derivedFrom":makeQuery(id+"F13.opLoft","SWEPT_EDGE",EDGE,{"disambiguationData":[OSD([sQuery(id+"F5.wireOp",EDGE,"E11"),sQuery(id+"F5.wireOp",EDGE,"E12"),sQuery(id+"F10.wireOp",EDGE,"E31"),sQuery(id+"F10.wireOp",EDGE,"E32")])]}),"instanceName":"16"});
            var Q84;
            Q84=makeQuery(id+"F16.opPattern","COPY",EDGE,{"derivedFrom":makeQuery(id+"F13.opLoft","SWEPT_EDGE",EDGE,{"disambiguationData":[OSD([sQuery(id+"F5.wireOp",EDGE,"E11"),sQuery(id+"F5.wireOp",EDGE,"E12"),sQuery(id+"F10.wireOp",EDGE,"E31"),sQuery(id+"F10.wireOp",EDGE,"E32")])]}),"instanceName":"15"});
            var Q85;
            Q85=makeQuery(id+"F16.opPattern","COPY",EDGE,{"derivedFrom":makeQuery(id+"F13.opLoft","SWEPT_EDGE",EDGE,{"disambiguationData":[OSD([sQuery(id+"F5.wireOp",EDGE,"E11"),sQuery(id+"F5.wireOp",EDGE,"E12"),sQuery(id+"F10.wireOp",EDGE,"E31"),sQuery(id+"F10.wireOp",EDGE,"E32")])]}),"instanceName":"14"});
            var Q86;
            Q86=makeQuery(id+"F16.opPattern","COPY",EDGE,{"derivedFrom":makeQuery(id+"F13.opLoft","SWEPT_EDGE",EDGE,{"disambiguationData":[OSD([sQuery(id+"F5.wireOp",EDGE,"E11"),sQuery(id+"F5.wireOp",EDGE,"E12"),sQuery(id+"F10.wireOp",EDGE,"E31"),sQuery(id+"F10.wireOp",EDGE,"E32")])]}),"instanceName":"13"});
            var Q87;
            Q87=makeQuery(id+"F16.opPattern","COPY",EDGE,{"derivedFrom":makeQuery(id+"F13.opLoft","SWEPT_EDGE",EDGE,{"disambiguationData":[OSD([sQuery(id+"F5.wireOp",EDGE,"E11"),sQuery(id+"F5.wireOp",EDGE,"E12"),sQuery(id+"F10.wireOp",EDGE,"E31"),sQuery(id+"F10.wireOp",EDGE,"E32")])]}),"instanceName":"12"});
            var Q88;
            Q88=makeQuery(id+"F16.opPattern","COPY",EDGE,{"derivedFrom":makeQuery(id+"F13.opLoft","SWEPT_EDGE",EDGE,{"disambiguationData":[OSD([sQuery(id+"F5.wireOp",EDGE,"E11"),sQuery(id+"F5.wireOp",EDGE,"E12"),sQuery(id+"F10.wireOp",EDGE,"E31"),sQuery(id+"F10.wireOp",EDGE,"E32")])]}),"instanceName":"11"});
            var Q89;
            Q89=makeQuery(id+"F16.opPattern","COPY",EDGE,{"derivedFrom":makeQuery(id+"F13.opLoft","SWEPT_EDGE",EDGE,{"disambiguationData":[OSD([sQuery(id+"F5.wireOp",EDGE,"E11"),sQuery(id+"F5.wireOp",EDGE,"E12"),sQuery(id+"F10.wireOp",EDGE,"E31"),sQuery(id+"F10.wireOp",EDGE,"E32")])]}),"instanceName":"10"});
            var Q90;
            Q90=makeQuery(id+"F16.opPattern","COPY",EDGE,{"derivedFrom":makeQuery(id+"F13.opLoft","SWEPT_EDGE",EDGE,{"disambiguationData":[OSD([sQuery(id+"F5.wireOp",EDGE,"E11"),sQuery(id+"F5.wireOp",EDGE,"E12"),sQuery(id+"F10.wireOp",EDGE,"E31"),sQuery(id+"F10.wireOp",EDGE,"E32")])]}),"instanceName":"9"});
            var Q91;
            Q91=makeQuery(id+"F16.opPattern","COPY",EDGE,{"derivedFrom":makeQuery(id+"F13.opLoft","SWEPT_EDGE",EDGE,{"disambiguationData":[OSD([sQuery(id+"F5.wireOp",EDGE,"E11"),sQuery(id+"F5.wireOp",EDGE,"E12"),sQuery(id+"F10.wireOp",EDGE,"E31"),sQuery(id+"F10.wireOp",EDGE,"E32")])]}),"instanceName":"8"});
            var Q92;
            Q92=makeQuery(id+"F16.opPattern","COPY",EDGE,{"derivedFrom":makeQuery(id+"F13.opLoft","SWEPT_EDGE",EDGE,{"disambiguationData":[OSD([sQuery(id+"F5.wireOp",EDGE,"E11"),sQuery(id+"F5.wireOp",EDGE,"E12"),sQuery(id+"F10.wireOp",EDGE,"E31"),sQuery(id+"F10.wireOp",EDGE,"E32")])]}),"instanceName":"7"});
            var Q93;
            Q93=makeQuery(id+"F16.opPattern","COPY",EDGE,{"derivedFrom":makeQuery(id+"F13.opLoft","SWEPT_EDGE",EDGE,{"disambiguationData":[OSD([sQuery(id+"F5.wireOp",EDGE,"E11"),sQuery(id+"F5.wireOp",EDGE,"E12"),sQuery(id+"F10.wireOp",EDGE,"E31"),sQuery(id+"F10.wireOp",EDGE,"E32")])]}),"instanceName":"6"});
            var Q94;
            Q94=makeQuery(id+"F16.opPattern","COPY",EDGE,{"derivedFrom":makeQuery(id+"F13.opLoft","SWEPT_EDGE",EDGE,{"disambiguationData":[OSD([sQuery(id+"F5.wireOp",EDGE,"E9"),sQuery(id+"F5.wireOp",EDGE,"E10"),sQuery(id+"F10.wireOp",EDGE,"E30"),sQuery(id+"F10.wireOp",EDGE,"E33")])]}),"instanceName":"6"});
            var Q95;
            Q95=makeQuery(id+"F16.opPattern","COPY",EDGE,{"derivedFrom":makeQuery(id+"F13.opLoft","SWEPT_EDGE",EDGE,{"disambiguationData":[OSD([sQuery(id+"F5.wireOp",EDGE,"E9"),sQuery(id+"F5.wireOp",EDGE,"E10"),sQuery(id+"F10.wireOp",EDGE,"E30"),sQuery(id+"F10.wireOp",EDGE,"E33")])]}),"instanceName":"7"});
            var Q96;
            Q96=makeQuery(id+"F16.opPattern","COPY",EDGE,{"derivedFrom":makeQuery(id+"F13.opLoft","SWEPT_EDGE",EDGE,{"disambiguationData":[OSD([sQuery(id+"F5.wireOp",EDGE,"E9"),sQuery(id+"F5.wireOp",EDGE,"E10"),sQuery(id+"F10.wireOp",EDGE,"E30"),sQuery(id+"F10.wireOp",EDGE,"E33")])]}),"instanceName":"8"});
            var Q97;
            Q97=makeQuery(id+"F16.opPattern","COPY",EDGE,{"derivedFrom":makeQuery(id+"F13.opLoft","SWEPT_EDGE",EDGE,{"disambiguationData":[OSD([sQuery(id+"F5.wireOp",EDGE,"E9"),sQuery(id+"F5.wireOp",EDGE,"E10"),sQuery(id+"F10.wireOp",EDGE,"E30"),sQuery(id+"F10.wireOp",EDGE,"E33")])]}),"instanceName":"9"});
            var Q98;
            Q98=makeQuery(id+"F16.opPattern","COPY",EDGE,{"derivedFrom":makeQuery(id+"F13.opLoft","SWEPT_EDGE",EDGE,{"disambiguationData":[OSD([sQuery(id+"F5.wireOp",EDGE,"E9"),sQuery(id+"F5.wireOp",EDGE,"E10"),sQuery(id+"F10.wireOp",EDGE,"E30"),sQuery(id+"F10.wireOp",EDGE,"E33")])]}),"instanceName":"10"});
            var Q99;
            Q99=makeQuery(id+"F16.opPattern","COPY",EDGE,{"derivedFrom":makeQuery(id+"F13.opLoft","SWEPT_EDGE",EDGE,{"disambiguationData":[OSD([sQuery(id+"F5.wireOp",EDGE,"E9"),sQuery(id+"F5.wireOp",EDGE,"E10"),sQuery(id+"F10.wireOp",EDGE,"E30"),sQuery(id+"F10.wireOp",EDGE,"E33")])]}),"instanceName":"11"});
            var Q100;
            Q100=makeQuery(id+"F16.opPattern","COPY",EDGE,{"derivedFrom":makeQuery(id+"F13.opLoft","SWEPT_EDGE",EDGE,{"disambiguationData":[OSD([sQuery(id+"F5.wireOp",EDGE,"E9"),sQuery(id+"F5.wireOp",EDGE,"E10"),sQuery(id+"F10.wireOp",EDGE,"E30"),sQuery(id+"F10.wireOp",EDGE,"E33")])]}),"instanceName":"12"});
            var Q101;
            Q101=makeQuery(id+"F16.opPattern","COPY",EDGE,{"derivedFrom":makeQuery(id+"F13.opLoft","SWEPT_EDGE",EDGE,{"disambiguationData":[OSD([sQuery(id+"F5.wireOp",EDGE,"E9"),sQuery(id+"F5.wireOp",EDGE,"E10"),sQuery(id+"F10.wireOp",EDGE,"E30"),sQuery(id+"F10.wireOp",EDGE,"E33")])]}),"instanceName":"13"});
            var Q102;
            Q102=makeQuery(id+"F16.opPattern","COPY",EDGE,{"derivedFrom":makeQuery(id+"F13.opLoft","SWEPT_EDGE",EDGE,{"disambiguationData":[OSD([sQuery(id+"F5.wireOp",EDGE,"E9"),sQuery(id+"F5.wireOp",EDGE,"E10"),sQuery(id+"F10.wireOp",EDGE,"E30"),sQuery(id+"F10.wireOp",EDGE,"E33")])]}),"instanceName":"14"});
            var Q103;
            Q103=makeQuery(id+"F16.opPattern","COPY",EDGE,{"derivedFrom":makeQuery(id+"F13.opLoft","SWEPT_EDGE",EDGE,{"disambiguationData":[OSD([sQuery(id+"F5.wireOp",EDGE,"E9"),sQuery(id+"F5.wireOp",EDGE,"E10"),sQuery(id+"F10.wireOp",EDGE,"E30"),sQuery(id+"F10.wireOp",EDGE,"E33")])]}),"instanceName":"15"});
            var Q104;
            Q104=makeQuery(id+"F16.opPattern","COPY",EDGE,{"derivedFrom":makeQuery(id+"F13.opLoft","SWEPT_EDGE",EDGE,{"disambiguationData":[OSD([sQuery(id+"F5.wireOp",EDGE,"E9"),sQuery(id+"F5.wireOp",EDGE,"E10"),sQuery(id+"F10.wireOp",EDGE,"E30"),sQuery(id+"F10.wireOp",EDGE,"E33")])]}),"instanceName":"16"});
            var Q105;
            Q105=makeQuery(id+"F16.opPattern","COPY",EDGE,{"derivedFrom":makeQuery(id+"F13.opLoft","SWEPT_EDGE",EDGE,{"disambiguationData":[OSD([sQuery(id+"F5.wireOp",EDGE,"E9"),sQuery(id+"F5.wireOp",EDGE,"E10"),sQuery(id+"F10.wireOp",EDGE,"E30"),sQuery(id+"F10.wireOp",EDGE,"E33")])]}),"instanceName":"17"});
            var Q106;
            Q106=makeQuery(id+"F13.opLoft","SWEPT_EDGE",EDGE,{"disambiguationData":[OSD([sQuery(id+"F5.wireOp",EDGE,"E9"),sQuery(id+"F5.wireOp",EDGE,"E10"),sQuery(id+"F10.wireOp",EDGE,"E30"),sQuery(id+"F10.wireOp",EDGE,"E33")])]});
            var Q107;
            Q107=makeQuery(id+"F16.opPattern","COPY",EDGE,{"derivedFrom":makeQuery(id+"F13.opLoft","SWEPT_EDGE",EDGE,{"disambiguationData":[OSD([sQuery(id+"F5.wireOp",EDGE,"E9"),sQuery(id+"F5.wireOp",EDGE,"E10"),sQuery(id+"F10.wireOp",EDGE,"E30"),sQuery(id+"F10.wireOp",EDGE,"E33")])]}),"instanceName":"1"});
            var Q108;
            Q108=makeQuery(id+"F16.opPattern","COPY",EDGE,{"derivedFrom":makeQuery(id+"F13.opLoft","SWEPT_EDGE",EDGE,{"disambiguationData":[OSD([sQuery(id+"F5.wireOp",EDGE,"E9"),sQuery(id+"F5.wireOp",EDGE,"E10"),sQuery(id+"F10.wireOp",EDGE,"E30"),sQuery(id+"F10.wireOp",EDGE,"E33")])]}),"instanceName":"2"});
            fillet(context, id + "F23", {"entities" : qUnion([Q0, Q1, Q2, Q3, Q4, Q5, Q6, Q7, Q8, Q9, Q10, Q11, Q12, Q13, Q14, Q15, Q16, Q17, Q18, Q19, Q20, Q21, Q22, Q23, Q24, Q25, Q26, Q27, Q28, Q29, Q30, Q31, Q32, Q33, Q34, Q35, Q36, Q37, Q38, Q39, Q40, Q41, Q42, Q43, Q44, Q45, Q46, Q47, Q48, Q49, Q50, Q51, Q52, Q53, Q54, Q55, Q56, Q57, Q58, Q59, Q60, Q61, Q62, Q63, Q64, Q65, Q66, Q67, Q68, Q69, Q70, Q71, Q72, Q73, Q74, Q75, Q76, Q77, Q78, Q79, Q80, Q81, Q82, Q83, Q84, Q85, Q86, Q87, Q88, Q89, Q90, Q91, Q92, Q93, Q94, Q95, Q96, Q97, Q98, Q99, Q100, Q101, Q102, Q103, Q104, Q105, Q106, Q107, Q108]), "radius" : 0.5 * mm, "tangentPropagation" : true, "allowEdgeOverflow" : false});
        }
    });
